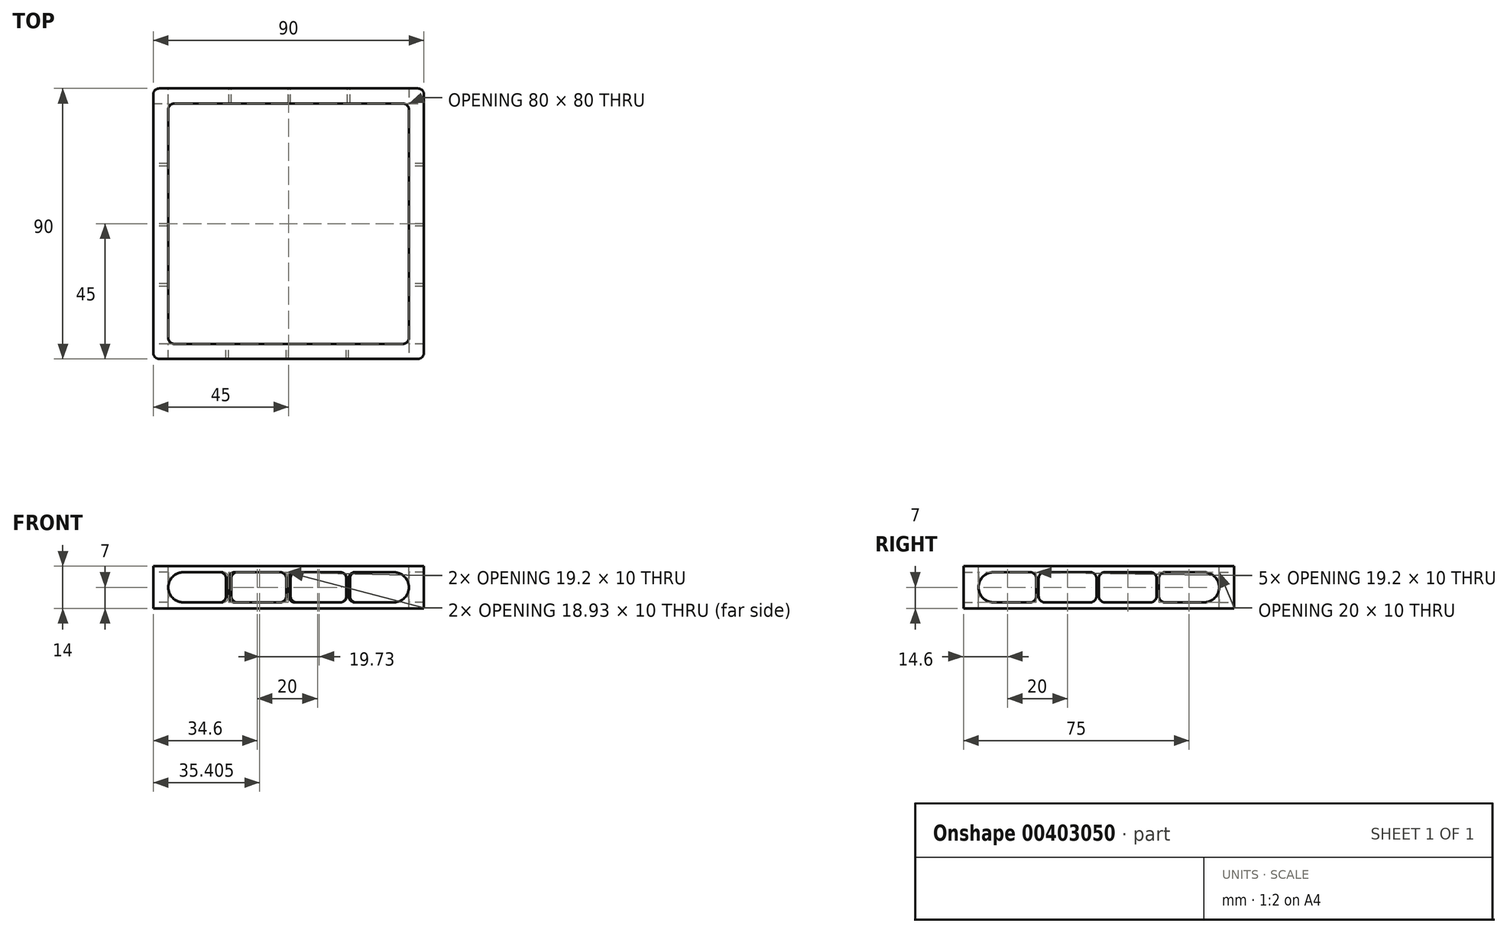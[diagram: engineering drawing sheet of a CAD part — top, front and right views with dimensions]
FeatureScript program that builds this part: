
annotation { "Feature Type Name" : "Feature", "Feature Type Description" : "" }
export const myFeature = defineFeature(function(context is Context, id is Id, definition is map)
    precondition{}
    {
        {
            var Q0;
            Q0=qCreatedBy(makeId("Front.planeOp"),FACE);
            var sketch = newSketch(context, id + "F0", { "sketchPlane" : qUnion([Q0])});
            skLineSegment(sketch, "E0.bottom", {"start": v(-45, 7) * mm, "end": v(45, 7) * mm});
            skLineSegment(sketch, "E0.top", {"start": v(-45, -7) * mm, "end": v(45, -7) * mm});
            skLineSegment(sketch, "E0.left", {"start": v(-45, 7) * mm, "end": v(-45, -7) * mm});
            skLineSegment(sketch, "E0.right", {"start": v(45, 7) * mm, "end": v(45, -7) * mm});
            skPoint(sketch, "E0.middle", {"position": v(0, 0) * mm});
            skSolve(sketch);
        }
        {
            var Q0;
            Q0 = qSketchRegion(id + "F0", true);
            extrude(context, id + "F1", {"entities" : qUnion([Q0]), "endBound" : BoundingType.SYMMETRIC, "depth" : 90 * mm});
        }
        {
            var Q0;
            Q0=makeQuery(id+"F1.opExtrude","CAP_FACE",FACE,{"disambiguationData":[OSD([sQuery(id+"F0.wireOp",EDGE,"E0.bottom"),sQuery(id+"F0.wireOp",EDGE,"E0.top"),sQuery(id+"F0.wireOp",EDGE,"E0.left"),sQuery(id+"F0.wireOp",EDGE,"E0.right")])],"isStart":false});
            var sketch = newSketch(context, id + "F2", { "sketchPlane" : qUnion([Q0])});
            skLineSegment(sketch, "E1.bottom", {"start": v(-40, 5) * mm, "end": v(40, 5) * mm});
            skLineSegment(sketch, "E1.top", {"start": v(-40, -5) * mm, "end": v(40, -5) * mm});
            skLineSegment(sketch, "E1.left", {"start": v(-40, 5) * mm, "end": v(-40, -5) * mm});
            skLineSegment(sketch, "E1.right", {"start": v(40, 5) * mm, "end": v(40, -5) * mm});
            skPoint(sketch, "E1.middle", {"position": v(0, 0) * mm});
            skSolve(sketch);
        }
        {
            var Q0;
            Q0 = qSketchRegion(id + "F2", true);
            extrude(context, id + "F3", {"entities" : qUnion([Q0]), "operationType" : NewBodyOperationType.REMOVE, "oppositeDirection" : true, "depth" : 90 * mm});
        }
        {
            var Q0;
            Q0=makeQuery(id+"F1.opExtrude","SWEPT_FACE",FACE,{"disambiguationData":[OSD([sQuery(id+"F0.wireOp",EDGE,"E0.right")])]});
            var sketch = newSketch(context, id + "F4", { "sketchPlane" : qUnion([Q0])});
            skLineSegment(sketch, "E2.bottom", {"start": v(-40, 5) * mm, "end": v(40, 5) * mm});
            skLineSegment(sketch, "E2.top", {"start": v(-40, -5) * mm, "end": v(40, -5) * mm});
            skLineSegment(sketch, "E2.left", {"start": v(-40, 5) * mm, "end": v(-40, -5) * mm});
            skLineSegment(sketch, "E2.right", {"start": v(40, 5) * mm, "end": v(40, -5) * mm});
            skPoint(sketch, "E2.middle", {"position": v(0, 0) * mm});
            skSolve(sketch);
        }
        {
            var Q0;
            Q0 = qSketchRegion(id + "F4", true);
            extrude(context, id + "F5", {"entities" : qUnion([Q0]), "operationType" : NewBodyOperationType.REMOVE, "oppositeDirection" : true, "depth" : 90 * mm});
        }
        {
            var Q0;
            Q0=makeQuery(id+"F1.opExtrude","SWEPT_FACE",FACE,{"disambiguationData":[OSD([sQuery(id+"F0.wireOp",EDGE,"E0.bottom")])]});
            var sketch = newSketch(context, id + "F6", { "sketchPlane" : qUnion([Q0])});
            skLineSegment(sketch, "E3.bottom", {"start": v(-40, 40) * mm, "end": v(40, 40) * mm});
            skLineSegment(sketch, "E3.top", {"start": v(-40, -40) * mm, "end": v(40, -40) * mm});
            skLineSegment(sketch, "E3.left", {"start": v(-40, 40) * mm, "end": v(-40, -40) * mm});
            skLineSegment(sketch, "E3.right", {"start": v(40, 40) * mm, "end": v(40, -40) * mm});
            skSolve(sketch);
        }
        {
            var Q0;
            Q0 = qSketchRegion(id + "F6", true);
            extrude(context, id + "F7", {"entities" : qUnion([Q0]), "operationType" : NewBodyOperationType.REMOVE, "oppositeDirection" : true, "depth" : 14 * mm});
        }
        {
            var Q0;
            {var subQ3=sQuery(id+"F6.wireOp",EDGE,"E3.bottom");var subQ4=sQuery(id+"F6.wireOp",EDGE,"E3.left");Q0=makeQuery(id+"F7.boolean.opBoolean","COPY",EDGE,{"disambiguationData":[TD([makeQuery(id+"F1.opExtrude","SWEPT_FACE",FACE,{"disambiguationData":[OSD([sQuery(id+"F0.wireOp",EDGE,"E0.bottom")])]})])],"derivedFrom":makeQuery(id+"F7.opExtrude","SWEPT_EDGE",EDGE,{"disambiguationData":[OSD([subQ3,subQ4])]})});}
            var Q1;
            {var subQ3=sQuery(id+"F6.wireOp",EDGE,"E3.bottom");var subQ4=sQuery(id+"F6.wireOp",EDGE,"E3.left");Q1=makeQuery(id+"F7.boolean.opBoolean","COPY",EDGE,{"disambiguationData":[TD([makeQuery(id+"F1.opExtrude","SWEPT_FACE",FACE,{"disambiguationData":[OSD([sQuery(id+"F0.wireOp",EDGE,"E0.top")])]})])],"derivedFrom":makeQuery(id+"F7.opExtrude","SWEPT_EDGE",EDGE,{"disambiguationData":[OSD([subQ3,subQ4])]})});}
            var Q2;
            {var subQ3=sQuery(id+"F6.wireOp",EDGE,"E3.top");var subQ4=sQuery(id+"F6.wireOp",EDGE,"E3.left");Q2=makeQuery(id+"F7.boolean.opBoolean","COPY",EDGE,{"disambiguationData":[TD([makeQuery(id+"F1.opExtrude","SWEPT_FACE",FACE,{"disambiguationData":[OSD([sQuery(id+"F0.wireOp",EDGE,"E0.top")])]})])],"derivedFrom":makeQuery(id+"F7.opExtrude","SWEPT_EDGE",EDGE,{"disambiguationData":[OSD([subQ3,subQ4])]})});}
            var Q3;
            {var subQ3=sQuery(id+"F6.wireOp",EDGE,"E3.top");var subQ4=sQuery(id+"F6.wireOp",EDGE,"E3.left");Q3=makeQuery(id+"F7.boolean.opBoolean","COPY",EDGE,{"disambiguationData":[TD([makeQuery(id+"F1.opExtrude","SWEPT_FACE",FACE,{"disambiguationData":[OSD([sQuery(id+"F0.wireOp",EDGE,"E0.bottom")])]})])],"derivedFrom":makeQuery(id+"F7.opExtrude","SWEPT_EDGE",EDGE,{"disambiguationData":[OSD([subQ3,subQ4])]})});}
            var Q4;
            {var subQ3=sQuery(id+"F6.wireOp",EDGE,"E3.right");var subQ4=sQuery(id+"F6.wireOp",EDGE,"E3.top");Q4=makeQuery(id+"F7.boolean.opBoolean","COPY",EDGE,{"disambiguationData":[TD([makeQuery(id+"F1.opExtrude","SWEPT_FACE",FACE,{"disambiguationData":[OSD([sQuery(id+"F0.wireOp",EDGE,"E0.bottom")])]})])],"derivedFrom":makeQuery(id+"F7.opExtrude","SWEPT_EDGE",EDGE,{"disambiguationData":[OSD([subQ4,subQ3])]})});}
            var Q5;
            {var subQ3=sQuery(id+"F6.wireOp",EDGE,"E3.top");var subQ4=sQuery(id+"F6.wireOp",EDGE,"E3.right");Q5=makeQuery(id+"F7.boolean.opBoolean","COPY",EDGE,{"disambiguationData":[TD([makeQuery(id+"F1.opExtrude","SWEPT_FACE",FACE,{"disambiguationData":[OSD([sQuery(id+"F0.wireOp",EDGE,"E0.top")])]})])],"derivedFrom":makeQuery(id+"F7.opExtrude","SWEPT_EDGE",EDGE,{"disambiguationData":[OSD([subQ3,subQ4])]})});}
            var Q6;
            {var subQ3=sQuery(id+"F6.wireOp",EDGE,"E3.right");var subQ4=sQuery(id+"F6.wireOp",EDGE,"E3.bottom");Q6=makeQuery(id+"F7.boolean.opBoolean","COPY",EDGE,{"disambiguationData":[TD([makeQuery(id+"F1.opExtrude","SWEPT_FACE",FACE,{"disambiguationData":[OSD([sQuery(id+"F0.wireOp",EDGE,"E0.bottom")])]})])],"derivedFrom":makeQuery(id+"F7.opExtrude","SWEPT_EDGE",EDGE,{"disambiguationData":[OSD([subQ4,subQ3])]})});}
            var Q7;
            {var subQ3=sQuery(id+"F6.wireOp",EDGE,"E3.bottom");var subQ4=sQuery(id+"F6.wireOp",EDGE,"E3.right");Q7=makeQuery(id+"F7.boolean.opBoolean","COPY",EDGE,{"disambiguationData":[TD([makeQuery(id+"F1.opExtrude","SWEPT_FACE",FACE,{"disambiguationData":[OSD([sQuery(id+"F0.wireOp",EDGE,"E0.top")])]})])],"derivedFrom":makeQuery(id+"F7.opExtrude","SWEPT_EDGE",EDGE,{"disambiguationData":[OSD([subQ3,subQ4])]})});}
            var Q8;
            Q8=makeQuery(id+"F1.opExtrude","CAP_EDGE",EDGE,{"disambiguationData":[OSD([sQuery(id+"F0.wireOp",EDGE,"E0.left")])],"isStart":false});
            var Q9;
            Q9=makeQuery(id+"F1.opExtrude","CAP_EDGE",EDGE,{"disambiguationData":[OSD([sQuery(id+"F0.wireOp",EDGE,"E0.right")])],"isStart":false});
            var Q10;
            Q10=makeQuery(id+"F1.opExtrude","CAP_EDGE",EDGE,{"disambiguationData":[OSD([sQuery(id+"F0.wireOp",EDGE,"E0.right")])],"isStart":true});
            var Q11;
            Q11=makeQuery(id+"F1.opExtrude","CAP_EDGE",EDGE,{"disambiguationData":[OSD([sQuery(id+"F0.wireOp",EDGE,"E0.left")])],"isStart":true});
            fillet(context, id + "F8", {"entities" : qUnion([Q0, Q1, Q2, Q3, Q4, Q5, Q6, Q7, Q8, Q9, Q10, Q11]), "radius" : 2 * mm, "allowEdgeOverflow" : false});
        }
        {
            var Q0;
            {var subQ0=sQuery(id+"F2.wireOp",EDGE,"E1.top");var subQ1=sQuery(id+"F2.wireOp",EDGE,"E1.right");Q0=makeQuery(id+"F5.boolean.opBoolean","SPLIT",EDGE,{"disambiguationData":[TD([makeQuery(id+"F5.opExtrude","SWEPT_FACE",FACE,{"disambiguationData":[OSD([sQuery(id+"F4.wireOp",EDGE,"E2.left")])]})])],"derivedFrom":makeQuery(id+"F3.boolean.opBoolean","COPY",EDGE,{"derivedFrom":makeQuery(id+"F3.opExtrude","SWEPT_EDGE",EDGE,{"disambiguationData":[OSD([subQ0,subQ1])]})})});}
            var Q1;
            {var subQ0=sQuery(id+"F2.wireOp",EDGE,"E1.bottom");var subQ1=sQuery(id+"F2.wireOp",EDGE,"E1.right");Q1=makeQuery(id+"F5.boolean.opBoolean","SPLIT",EDGE,{"disambiguationData":[TD([makeQuery(id+"F5.opExtrude","SWEPT_FACE",FACE,{"disambiguationData":[OSD([sQuery(id+"F4.wireOp",EDGE,"E2.left")])]})])],"derivedFrom":makeQuery(id+"F3.boolean.opBoolean","COPY",EDGE,{"derivedFrom":makeQuery(id+"F3.opExtrude","SWEPT_EDGE",EDGE,{"disambiguationData":[OSD([subQ0,subQ1])]})})});}
            var Q2;
            {var subQ0=sQuery(id+"F2.wireOp",EDGE,"E1.left");var subQ1=sQuery(id+"F2.wireOp",EDGE,"E1.top");Q2=makeQuery(id+"F5.boolean.opBoolean","SPLIT",EDGE,{"disambiguationData":[TD([makeQuery(id+"F5.opExtrude","SWEPT_FACE",FACE,{"disambiguationData":[OSD([sQuery(id+"F4.wireOp",EDGE,"E2.left")])]})])],"derivedFrom":makeQuery(id+"F3.boolean.opBoolean","COPY",EDGE,{"derivedFrom":makeQuery(id+"F3.opExtrude","SWEPT_EDGE",EDGE,{"disambiguationData":[OSD([subQ1,subQ0])]})})});}
            var Q3;
            {var subQ0=sQuery(id+"F2.wireOp",EDGE,"E1.left");var subQ1=sQuery(id+"F2.wireOp",EDGE,"E1.bottom");Q3=makeQuery(id+"F5.boolean.opBoolean","SPLIT",EDGE,{"disambiguationData":[TD([makeQuery(id+"F5.opExtrude","SWEPT_FACE",FACE,{"disambiguationData":[OSD([sQuery(id+"F4.wireOp",EDGE,"E2.left")])]})])],"derivedFrom":makeQuery(id+"F3.boolean.opBoolean","COPY",EDGE,{"derivedFrom":makeQuery(id+"F3.opExtrude","SWEPT_EDGE",EDGE,{"disambiguationData":[OSD([subQ1,subQ0])]})})});}
            var Q4;
            {var subQ0=sQuery(id+"F4.wireOp",EDGE,"E2.top");var subQ1=sQuery(id+"F4.wireOp",EDGE,"E2.left");Q4=makeQuery(id+"F5.boolean.opBoolean","COPY",EDGE,{"disambiguationData":[TD([makeQuery(id+"F1.opExtrude","SWEPT_FACE",FACE,{"disambiguationData":[OSD([sQuery(id+"F0.wireOp",EDGE,"E0.right")])]})])],"derivedFrom":makeQuery(id+"F5.opExtrude","SWEPT_EDGE",EDGE,{"disambiguationData":[OSD([subQ0,subQ1])]})});}
            var Q5;
            {var subQ0=sQuery(id+"F4.wireOp",EDGE,"E2.bottom");var subQ1=sQuery(id+"F4.wireOp",EDGE,"E2.left");Q5=makeQuery(id+"F5.boolean.opBoolean","COPY",EDGE,{"disambiguationData":[TD([makeQuery(id+"F1.opExtrude","SWEPT_FACE",FACE,{"disambiguationData":[OSD([sQuery(id+"F0.wireOp",EDGE,"E0.right")])]})])],"derivedFrom":makeQuery(id+"F5.opExtrude","SWEPT_EDGE",EDGE,{"disambiguationData":[OSD([subQ0,subQ1])]})});}
            var Q6;
            {var subQ0=sQuery(id+"F4.wireOp",EDGE,"E2.top");var subQ1=sQuery(id+"F4.wireOp",EDGE,"E2.right");Q6=makeQuery(id+"F5.boolean.opBoolean","COPY",EDGE,{"disambiguationData":[TD([makeQuery(id+"F1.opExtrude","SWEPT_FACE",FACE,{"disambiguationData":[OSD([sQuery(id+"F0.wireOp",EDGE,"E0.right")])]})])],"derivedFrom":makeQuery(id+"F5.opExtrude","SWEPT_EDGE",EDGE,{"disambiguationData":[OSD([subQ0,subQ1])]})});}
            var Q7;
            {var subQ0=sQuery(id+"F4.wireOp",EDGE,"E2.bottom");var subQ1=sQuery(id+"F4.wireOp",EDGE,"E2.right");Q7=makeQuery(id+"F5.boolean.opBoolean","COPY",EDGE,{"disambiguationData":[TD([makeQuery(id+"F1.opExtrude","SWEPT_FACE",FACE,{"disambiguationData":[OSD([sQuery(id+"F0.wireOp",EDGE,"E0.right")])]})])],"derivedFrom":makeQuery(id+"F5.opExtrude","SWEPT_EDGE",EDGE,{"disambiguationData":[OSD([subQ0,subQ1])]})});}
            var Q8;
            {var subQ0=sQuery(id+"F2.wireOp",EDGE,"E1.right");var subQ1=sQuery(id+"F2.wireOp",EDGE,"E1.top");Q8=makeQuery(id+"F5.boolean.opBoolean","SPLIT",EDGE,{"disambiguationData":[TD([makeQuery(id+"F5.opExtrude","SWEPT_FACE",FACE,{"disambiguationData":[OSD([sQuery(id+"F4.wireOp",EDGE,"E2.right")])]})])],"derivedFrom":makeQuery(id+"F3.boolean.opBoolean","COPY",EDGE,{"derivedFrom":makeQuery(id+"F3.opExtrude","SWEPT_EDGE",EDGE,{"disambiguationData":[OSD([subQ1,subQ0])]})})});}
            var Q9;
            {var subQ0=sQuery(id+"F2.wireOp",EDGE,"E1.right");var subQ1=sQuery(id+"F2.wireOp",EDGE,"E1.bottom");Q9=makeQuery(id+"F5.boolean.opBoolean","SPLIT",EDGE,{"disambiguationData":[TD([makeQuery(id+"F5.opExtrude","SWEPT_FACE",FACE,{"disambiguationData":[OSD([sQuery(id+"F4.wireOp",EDGE,"E2.right")])]})])],"derivedFrom":makeQuery(id+"F3.boolean.opBoolean","COPY",EDGE,{"derivedFrom":makeQuery(id+"F3.opExtrude","SWEPT_EDGE",EDGE,{"disambiguationData":[OSD([subQ1,subQ0])]})})});}
            var Q10;
            {var subQ0=sQuery(id+"F2.wireOp",EDGE,"E1.top");var subQ1=sQuery(id+"F2.wireOp",EDGE,"E1.left");Q10=makeQuery(id+"F5.boolean.opBoolean","SPLIT",EDGE,{"disambiguationData":[TD([makeQuery(id+"F5.opExtrude","SWEPT_FACE",FACE,{"disambiguationData":[OSD([sQuery(id+"F4.wireOp",EDGE,"E2.right")])]})])],"derivedFrom":makeQuery(id+"F3.boolean.opBoolean","COPY",EDGE,{"derivedFrom":makeQuery(id+"F3.opExtrude","SWEPT_EDGE",EDGE,{"disambiguationData":[OSD([subQ0,subQ1])]})})});}
            var Q11;
            {var subQ0=sQuery(id+"F4.wireOp",EDGE,"E2.top");var subQ1=sQuery(id+"F4.wireOp",EDGE,"E2.right");Q11=makeQuery(id+"F5.boolean.opBoolean","COPY",EDGE,{"disambiguationData":[TD([makeQuery(id+"F1.opExtrude","SWEPT_FACE",FACE,{"disambiguationData":[OSD([sQuery(id+"F0.wireOp",EDGE,"E0.left")])]})])],"derivedFrom":makeQuery(id+"F5.opExtrude","SWEPT_EDGE",EDGE,{"disambiguationData":[OSD([subQ0,subQ1])]})});}
            var Q12;
            {var subQ0=sQuery(id+"F4.wireOp",EDGE,"E2.top");var subQ1=sQuery(id+"F4.wireOp",EDGE,"E2.left");Q12=makeQuery(id+"F5.boolean.opBoolean","COPY",EDGE,{"disambiguationData":[TD([makeQuery(id+"F1.opExtrude","SWEPT_FACE",FACE,{"disambiguationData":[OSD([sQuery(id+"F0.wireOp",EDGE,"E0.left")])]})])],"derivedFrom":makeQuery(id+"F5.opExtrude","SWEPT_EDGE",EDGE,{"disambiguationData":[OSD([subQ0,subQ1])]})});}
            var Q13;
            {var subQ0=sQuery(id+"F4.wireOp",EDGE,"E2.bottom");var subQ1=sQuery(id+"F4.wireOp",EDGE,"E2.left");Q13=makeQuery(id+"F5.boolean.opBoolean","COPY",EDGE,{"disambiguationData":[TD([makeQuery(id+"F1.opExtrude","SWEPT_FACE",FACE,{"disambiguationData":[OSD([sQuery(id+"F0.wireOp",EDGE,"E0.left")])]})])],"derivedFrom":makeQuery(id+"F5.opExtrude","SWEPT_EDGE",EDGE,{"disambiguationData":[OSD([subQ0,subQ1])]})});}
            var Q14;
            {var subQ0=sQuery(id+"F2.wireOp",EDGE,"E1.bottom");var subQ1=sQuery(id+"F2.wireOp",EDGE,"E1.left");Q14=makeQuery(id+"F5.boolean.opBoolean","SPLIT",EDGE,{"disambiguationData":[TD([makeQuery(id+"F5.opExtrude","SWEPT_FACE",FACE,{"disambiguationData":[OSD([sQuery(id+"F4.wireOp",EDGE,"E2.right")])]})])],"derivedFrom":makeQuery(id+"F3.boolean.opBoolean","COPY",EDGE,{"derivedFrom":makeQuery(id+"F3.opExtrude","SWEPT_EDGE",EDGE,{"disambiguationData":[OSD([subQ0,subQ1])]})})});}
            var Q15;
            {var subQ0=sQuery(id+"F4.wireOp",EDGE,"E2.bottom");var subQ1=sQuery(id+"F4.wireOp",EDGE,"E2.right");Q15=makeQuery(id+"F5.boolean.opBoolean","COPY",EDGE,{"disambiguationData":[TD([makeQuery(id+"F1.opExtrude","SWEPT_FACE",FACE,{"disambiguationData":[OSD([sQuery(id+"F0.wireOp",EDGE,"E0.left")])]})])],"derivedFrom":makeQuery(id+"F5.opExtrude","SWEPT_EDGE",EDGE,{"disambiguationData":[OSD([subQ0,subQ1])]})});}
            fillet(context, id + "F9", {"entities" : qUnion([Q0, Q1, Q2, Q3, Q4, Q5, Q6, Q7, Q8, Q9, Q10, Q11, Q12, Q13, Q14, Q15]), "radius" : 5 * mm, "tangentPropagation" : true, "allowEdgeOverflow" : false});
        }
        {
            var Q0;
            Q0=makeQuery(id+"F1.opExtrude","SWEPT_FACE",FACE,{"disambiguationData":[OSD([sQuery(id+"F0.wireOp",EDGE,"E0.bottom")])]});
            var sketch = newSketch(context, id + "F10", { "sketchPlane" : qUnion([Q0])});
            skLineSegment(sketch, "E4.bottom", {"start": v(19.2, -40) * mm, "end": v(20, -40) * mm});
            skLineSegment(sketch, "E4.top", {"start": v(19.2, -45) * mm, "end": v(20, -45) * mm});
            skLineSegment(sketch, "E4.left", {"start": v(19.2, -40) * mm, "end": v(19.2, -45) * mm});
            skLineSegment(sketch, "E4.right", {"start": v(20, -40) * mm, "end": v(20, -45) * mm});
            skLineSegment(sketch, "E5.1.0.0", {"start": v(-0.8, -40) * mm, "end": v(-0.8, -45) * mm});
            skLineSegment(sketch, "E5.1.0.1", {"start": v(0, -40) * mm, "end": v(0, -45) * mm});
            skLineSegment(sketch, "E5.1.0.2", {"start": v(-0.8, -45) * mm, "end": v(0, -45) * mm});
            skLineSegment(sketch, "E5.1.0.3", {"start": v(-0.8, -40) * mm, "end": v(0, -40) * mm});
            skLineSegment(sketch, "E5.2.0.0", {"start": v(-20.8, -40) * mm, "end": v(-20.8, -45) * mm});
            skLineSegment(sketch, "E5.2.0.1", {"start": v(-20, -40) * mm, "end": v(-20, -45) * mm});
            skLineSegment(sketch, "E5.2.0.2", {"start": v(-20.8, -45) * mm, "end": v(-20, -45) * mm});
            skLineSegment(sketch, "E5.2.0.3", {"start": v(-20.8, -40) * mm, "end": v(-20, -40) * mm});
            skLineSegment(sketch, "E5.direction1", {"start": v(19.2, -45) * mm, "end": v(-0.8, -45) * mm, "construction": true});
            skLineSegment(sketch, "E6.0.1.0", {"start": v(19.6, 40) * mm, "end": v(-0.13, 40) * mm, "construction": true});
            skLineSegment(sketch, "E6.0.1.1", {"start": v(19.6, 40) * mm, "end": v(20.4, 40) * mm});
            skLineSegment(sketch, "E6.0.1.2", {"start": v(19.6, 45) * mm, "end": v(19.6, 40) * mm});
            skLineSegment(sketch, "E6.0.1.3", {"start": v(20.4, 45) * mm, "end": v(20.4, 40) * mm});
            skLineSegment(sketch, "E6.0.1.4", {"start": v(-29.6, 40) * mm, "end": v(-29.2, 40) * mm});
            skLineSegment(sketch, "E6.0.1.5", {"start": v(-29.6, 45) * mm, "end": v(-29.2, 45) * mm});
            skLineSegment(sketch, "E6.0.1.6", {"start": v(19.6, 45) * mm, "end": v(20.4, 45) * mm});
            skLineSegment(sketch, "E6.0.1.7", {"start": v(0.67, 45) * mm, "end": v(0.67, 40) * mm});
            skLineSegment(sketch, "E6.0.1.8", {"start": v(-0.13, 45) * mm, "end": v(0.67, 45) * mm});
            skLineSegment(sketch, "E6.0.1.9", {"start": v(-19.06, 45) * mm, "end": v(-19.06, 40) * mm});
            skLineSegment(sketch, "E6.0.1.10", {"start": v(-19.86, 40) * mm, "end": v(-19.06, 40) * mm});
            skLineSegment(sketch, "E6.0.1.11", {"start": v(-19.86, 45) * mm, "end": v(-19.06, 45) * mm});
            skLineSegment(sketch, "E6.0.1.14", {"start": v(-0.13, 45) * mm, "end": v(-0.13, 40) * mm});
            skLineSegment(sketch, "E6.0.1.15", {"start": v(-0.13, 40) * mm, "end": v(0.67, 40) * mm});
            skLineSegment(sketch, "E6.0.1.16", {"start": v(-19.86, 45) * mm, "end": v(-19.86, 40) * mm});
            skLineSegment(sketch, "E6.direction1", {"start": v(-29.6, -45) * mm, "end": v(-5, -45) * mm, "construction": true});
            skLineSegment(sketch, "E7.bottom", {"start": v(40, 19.2) * mm, "end": v(45, 19.2) * mm});
            skLineSegment(sketch, "E7.top", {"start": v(40, 20) * mm, "end": v(45, 20) * mm});
            skLineSegment(sketch, "E7.left", {"start": v(40, 19.2) * mm, "end": v(40, 20) * mm});
            skLineSegment(sketch, "E7.right", {"start": v(45, 19.2) * mm, "end": v(45, 20) * mm});
            skLineSegment(sketch, "E8.0.1.0", {"start": v(40, 0) * mm, "end": v(45, 0) * mm});
            skLineSegment(sketch, "E8.0.1.1", {"start": v(40, -0.8) * mm, "end": v(45, -0.8) * mm});
            skLineSegment(sketch, "E8.0.1.2", {"start": v(45, -0.8) * mm, "end": v(45, 0) * mm});
            skLineSegment(sketch, "E8.0.1.3", {"start": v(40, -0.8) * mm, "end": v(40, 0) * mm});
            skLineSegment(sketch, "E8.0.2.0", {"start": v(40, -20) * mm, "end": v(45, -20) * mm});
            skLineSegment(sketch, "E8.0.2.1", {"start": v(40, -20.8) * mm, "end": v(45, -20.8) * mm});
            skLineSegment(sketch, "E8.0.2.2", {"start": v(45, -20.8) * mm, "end": v(45, -20) * mm});
            skLineSegment(sketch, "E8.0.2.3", {"start": v(40, -20.8) * mm, "end": v(40, -20) * mm});
            skLineSegment(sketch, "E8.1.0.0", {"start": v(-45, 20) * mm, "end": v(-40, 20) * mm});
            skLineSegment(sketch, "E8.1.0.1", {"start": v(-45, 19.2) * mm, "end": v(-40, 19.2) * mm});
            skLineSegment(sketch, "E8.1.0.2", {"start": v(-40, 19.2) * mm, "end": v(-40, 20) * mm});
            skLineSegment(sketch, "E8.1.0.3", {"start": v(-45, 19.2) * mm, "end": v(-45, 20) * mm});
            skLineSegment(sketch, "E8.1.1.0", {"start": v(-45, 0) * mm, "end": v(-40, 0) * mm});
            skLineSegment(sketch, "E8.1.1.1", {"start": v(-45, -0.8) * mm, "end": v(-40, -0.8) * mm});
            skLineSegment(sketch, "E8.1.1.2", {"start": v(-40, -0.8) * mm, "end": v(-40, 0) * mm});
            skLineSegment(sketch, "E8.1.1.3", {"start": v(-45, -0.8) * mm, "end": v(-45, 0) * mm});
            skLineSegment(sketch, "E8.1.2.0", {"start": v(-45, -20) * mm, "end": v(-40, -20) * mm});
            skLineSegment(sketch, "E8.1.2.1", {"start": v(-45, -20.8) * mm, "end": v(-40, -20.8) * mm});
            skLineSegment(sketch, "E8.1.2.2", {"start": v(-40, -20.8) * mm, "end": v(-40, -20) * mm});
            skLineSegment(sketch, "E8.1.2.3", {"start": v(-45, -20.8) * mm, "end": v(-45, -20) * mm});
            skLineSegment(sketch, "E8.direction1", {"start": v(40, 19.2) * mm, "end": v(-45, 19.2) * mm, "construction": true});
            skLineSegment(sketch, "E8.direction2", {"start": v(40, 19.2) * mm, "end": v(40, -0.8) * mm, "construction": true});
            skSolve(sketch);
        }
        {
            var Q0;
            Q0 = qSketchRegion(id + "F10", true);
            extrude(context, id + "F11", {"entities" : qUnion([Q0]), "operationType" : NewBodyOperationType.ADD, "oppositeDirection" : true, "depth" : 14 * mm});
        }
        {
            var Q0;
            {var subQ1=makeQuery(id+"F5.opExtrude","SWEPT_FACE",FACE,{"disambiguationData":[OSD([sQuery(id+"F4.wireOp",EDGE,"E2.top")])]});var subQ2=makeQuery(id+"F3.boolean.opBoolean","COPY",FACE,{"derivedFrom":makeQuery(id+"F3.opExtrude","SWEPT_FACE",FACE,{"disambiguationData":[OSD([sQuery(id+"F2.wireOp",EDGE,"E1.top")])]})});var subQ3=sQuery(id+"F0.wireOp",EDGE,"E0.left");var subQ4=makeQuery(id+"F1.opExtrude","SWEPT_FACE",FACE,{"disambiguationData":[OSD([subQ3])]});var subQ14=makeQuery(id+"F5.boolean.opBoolean","MERGE",FACE,{"derivedFrom":[subQ2,subQ1]});var subQ16=sQuery(id+"F0.wireOp",EDGE,"E0.right");var subQ17=makeQuery(id+"F1.opExtrude","SWEPT_FACE",FACE,{"disambiguationData":[OSD([subQ16])]});var subQ21=sQuery(id+"F0.wireOp",EDGE,"E0.top");var subQ22=sQuery(id+"F0.wireOp",EDGE,"E0.bottom");Q0=makeQuery(id+"F11.boolean.opBoolean","INTERSECT",EDGE,{"derivedFrom":[makeQuery(id+"F9.opFillet","SPLIT",FACE,{"disambiguationData":[OD(0.0)],"derivedFrom":makeQuery(id+"F8.opFillet","MERGE",FACE,{"derivedFrom":[makeQuery(id+"F7.boolean.opBoolean","SPLIT",FACE,{"disambiguationData":[TD([makeQuery(id+"F1.opExtrude","CAP_FACE",FACE,{"disambiguationData":[OSD([subQ22,subQ21,subQ3,subQ16])],"isStart":false})])],"derivedFrom":subQ14}),makeQuery(id+"F7.boolean.opBoolean","SPLIT",FACE,{"disambiguationData":[TD([makeQuery(id+"F1.opExtrude","CAP_FACE",FACE,{"disambiguationData":[OSD([subQ22,subQ21,subQ3,subQ16])],"isStart":true})])],"derivedFrom":subQ14}),makeQuery(id+"F7.boolean.opBoolean","SPLIT",FACE,{"disambiguationData":[TD([subQ17])],"derivedFrom":subQ14}),makeQuery(id+"F7.boolean.opBoolean","SPLIT",FACE,{"disambiguationData":[TD([subQ4])],"derivedFrom":subQ14})]})}),makeQuery(id+"F11.opExtrude","SWEPT_FACE",FACE,{"disambiguationData":[OSD([sQuery(id+"F10.wireOp",EDGE,"E4.right")])]})]});}
            var Q1;
            {var subQ1=makeQuery(id+"F5.opExtrude","SWEPT_FACE",FACE,{"disambiguationData":[OSD([sQuery(id+"F4.wireOp",EDGE,"E2.top")])]});var subQ2=makeQuery(id+"F3.boolean.opBoolean","COPY",FACE,{"derivedFrom":makeQuery(id+"F3.opExtrude","SWEPT_FACE",FACE,{"disambiguationData":[OSD([sQuery(id+"F2.wireOp",EDGE,"E1.top")])]})});var subQ3=sQuery(id+"F0.wireOp",EDGE,"E0.left");var subQ4=makeQuery(id+"F1.opExtrude","SWEPT_FACE",FACE,{"disambiguationData":[OSD([subQ3])]});var subQ14=makeQuery(id+"F5.boolean.opBoolean","MERGE",FACE,{"derivedFrom":[subQ2,subQ1]});var subQ16=sQuery(id+"F0.wireOp",EDGE,"E0.right");var subQ17=makeQuery(id+"F1.opExtrude","SWEPT_FACE",FACE,{"disambiguationData":[OSD([subQ16])]});var subQ21=sQuery(id+"F0.wireOp",EDGE,"E0.top");var subQ22=sQuery(id+"F0.wireOp",EDGE,"E0.bottom");Q1=makeQuery(id+"F11.boolean.opBoolean","INTERSECT",EDGE,{"derivedFrom":[makeQuery(id+"F9.opFillet","SPLIT",FACE,{"disambiguationData":[OD(0.0)],"derivedFrom":makeQuery(id+"F8.opFillet","MERGE",FACE,{"derivedFrom":[makeQuery(id+"F7.boolean.opBoolean","SPLIT",FACE,{"disambiguationData":[TD([makeQuery(id+"F1.opExtrude","CAP_FACE",FACE,{"disambiguationData":[OSD([subQ22,subQ21,subQ3,subQ16])],"isStart":false})])],"derivedFrom":subQ14}),makeQuery(id+"F7.boolean.opBoolean","SPLIT",FACE,{"disambiguationData":[TD([makeQuery(id+"F1.opExtrude","CAP_FACE",FACE,{"disambiguationData":[OSD([subQ22,subQ21,subQ3,subQ16])],"isStart":true})])],"derivedFrom":subQ14}),makeQuery(id+"F7.boolean.opBoolean","SPLIT",FACE,{"disambiguationData":[TD([subQ17])],"derivedFrom":subQ14}),makeQuery(id+"F7.boolean.opBoolean","SPLIT",FACE,{"disambiguationData":[TD([subQ4])],"derivedFrom":subQ14})]})}),makeQuery(id+"F11.opExtrude","SWEPT_FACE",FACE,{"disambiguationData":[OSD([sQuery(id+"F10.wireOp",EDGE,"E5.1.0.1")])]})]});}
            var Q2;
            {var subQ1=makeQuery(id+"F5.opExtrude","SWEPT_FACE",FACE,{"disambiguationData":[OSD([sQuery(id+"F4.wireOp",EDGE,"E2.top")])]});var subQ2=makeQuery(id+"F3.boolean.opBoolean","COPY",FACE,{"derivedFrom":makeQuery(id+"F3.opExtrude","SWEPT_FACE",FACE,{"disambiguationData":[OSD([sQuery(id+"F2.wireOp",EDGE,"E1.top")])]})});var subQ3=sQuery(id+"F0.wireOp",EDGE,"E0.left");var subQ4=makeQuery(id+"F1.opExtrude","SWEPT_FACE",FACE,{"disambiguationData":[OSD([subQ3])]});var subQ14=makeQuery(id+"F5.boolean.opBoolean","MERGE",FACE,{"derivedFrom":[subQ2,subQ1]});var subQ16=sQuery(id+"F0.wireOp",EDGE,"E0.right");var subQ17=makeQuery(id+"F1.opExtrude","SWEPT_FACE",FACE,{"disambiguationData":[OSD([subQ16])]});var subQ21=sQuery(id+"F0.wireOp",EDGE,"E0.top");var subQ22=sQuery(id+"F0.wireOp",EDGE,"E0.bottom");Q2=makeQuery(id+"F11.boolean.opBoolean","INTERSECT",EDGE,{"derivedFrom":[makeQuery(id+"F9.opFillet","SPLIT",FACE,{"disambiguationData":[OD(0.0)],"derivedFrom":makeQuery(id+"F8.opFillet","MERGE",FACE,{"derivedFrom":[makeQuery(id+"F7.boolean.opBoolean","SPLIT",FACE,{"disambiguationData":[TD([makeQuery(id+"F1.opExtrude","CAP_FACE",FACE,{"disambiguationData":[OSD([subQ22,subQ21,subQ3,subQ16])],"isStart":false})])],"derivedFrom":subQ14}),makeQuery(id+"F7.boolean.opBoolean","SPLIT",FACE,{"disambiguationData":[TD([makeQuery(id+"F1.opExtrude","CAP_FACE",FACE,{"disambiguationData":[OSD([subQ22,subQ21,subQ3,subQ16])],"isStart":true})])],"derivedFrom":subQ14}),makeQuery(id+"F7.boolean.opBoolean","SPLIT",FACE,{"disambiguationData":[TD([subQ17])],"derivedFrom":subQ14}),makeQuery(id+"F7.boolean.opBoolean","SPLIT",FACE,{"disambiguationData":[TD([subQ4])],"derivedFrom":subQ14})]})}),makeQuery(id+"F11.opExtrude","SWEPT_FACE",FACE,{"disambiguationData":[OSD([sQuery(id+"F10.wireOp",EDGE,"E5.2.0.1")])]})]});}
            var Q3;
            {var subQ1=makeQuery(id+"F5.opExtrude","SWEPT_FACE",FACE,{"disambiguationData":[OSD([sQuery(id+"F4.wireOp",EDGE,"E2.top")])]});var subQ2=makeQuery(id+"F3.boolean.opBoolean","COPY",FACE,{"derivedFrom":makeQuery(id+"F3.opExtrude","SWEPT_FACE",FACE,{"disambiguationData":[OSD([sQuery(id+"F2.wireOp",EDGE,"E1.top")])]})});var subQ3=sQuery(id+"F0.wireOp",EDGE,"E0.left");var subQ4=makeQuery(id+"F1.opExtrude","SWEPT_FACE",FACE,{"disambiguationData":[OSD([subQ3])]});var subQ14=makeQuery(id+"F5.boolean.opBoolean","MERGE",FACE,{"derivedFrom":[subQ2,subQ1]});var subQ16=sQuery(id+"F0.wireOp",EDGE,"E0.right");var subQ17=makeQuery(id+"F1.opExtrude","SWEPT_FACE",FACE,{"disambiguationData":[OSD([subQ16])]});var subQ21=sQuery(id+"F0.wireOp",EDGE,"E0.top");var subQ22=sQuery(id+"F0.wireOp",EDGE,"E0.bottom");Q3=makeQuery(id+"F11.boolean.opBoolean","INTERSECT",EDGE,{"derivedFrom":[makeQuery(id+"F9.opFillet","SPLIT",FACE,{"disambiguationData":[OD(1.0)],"derivedFrom":makeQuery(id+"F8.opFillet","MERGE",FACE,{"derivedFrom":[makeQuery(id+"F7.boolean.opBoolean","SPLIT",FACE,{"disambiguationData":[TD([makeQuery(id+"F1.opExtrude","CAP_FACE",FACE,{"disambiguationData":[OSD([subQ22,subQ21,subQ3,subQ16])],"isStart":false})])],"derivedFrom":subQ14}),makeQuery(id+"F7.boolean.opBoolean","SPLIT",FACE,{"disambiguationData":[TD([makeQuery(id+"F1.opExtrude","CAP_FACE",FACE,{"disambiguationData":[OSD([subQ22,subQ21,subQ3,subQ16])],"isStart":true})])],"derivedFrom":subQ14}),makeQuery(id+"F7.boolean.opBoolean","SPLIT",FACE,{"disambiguationData":[TD([subQ17])],"derivedFrom":subQ14}),makeQuery(id+"F7.boolean.opBoolean","SPLIT",FACE,{"disambiguationData":[TD([subQ4])],"derivedFrom":subQ14})]})}),makeQuery(id+"F11.opExtrude","SWEPT_FACE",FACE,{"disambiguationData":[OSD([sQuery(id+"F10.wireOp",EDGE,"E6.0.1.9")])]})]});}
            var Q4;
            {var subQ1=makeQuery(id+"F5.opExtrude","SWEPT_FACE",FACE,{"disambiguationData":[OSD([sQuery(id+"F4.wireOp",EDGE,"E2.top")])]});var subQ2=makeQuery(id+"F3.boolean.opBoolean","COPY",FACE,{"derivedFrom":makeQuery(id+"F3.opExtrude","SWEPT_FACE",FACE,{"disambiguationData":[OSD([sQuery(id+"F2.wireOp",EDGE,"E1.top")])]})});var subQ3=sQuery(id+"F0.wireOp",EDGE,"E0.left");var subQ4=makeQuery(id+"F1.opExtrude","SWEPT_FACE",FACE,{"disambiguationData":[OSD([subQ3])]});var subQ14=makeQuery(id+"F5.boolean.opBoolean","MERGE",FACE,{"derivedFrom":[subQ2,subQ1]});var subQ16=sQuery(id+"F0.wireOp",EDGE,"E0.right");var subQ17=makeQuery(id+"F1.opExtrude","SWEPT_FACE",FACE,{"disambiguationData":[OSD([subQ16])]});var subQ21=sQuery(id+"F0.wireOp",EDGE,"E0.top");var subQ22=sQuery(id+"F0.wireOp",EDGE,"E0.bottom");Q4=makeQuery(id+"F11.boolean.opBoolean","INTERSECT",EDGE,{"derivedFrom":[makeQuery(id+"F9.opFillet","SPLIT",FACE,{"disambiguationData":[OD(1.0)],"derivedFrom":makeQuery(id+"F8.opFillet","MERGE",FACE,{"derivedFrom":[makeQuery(id+"F7.boolean.opBoolean","SPLIT",FACE,{"disambiguationData":[TD([makeQuery(id+"F1.opExtrude","CAP_FACE",FACE,{"disambiguationData":[OSD([subQ22,subQ21,subQ3,subQ16])],"isStart":false})])],"derivedFrom":subQ14}),makeQuery(id+"F7.boolean.opBoolean","SPLIT",FACE,{"disambiguationData":[TD([makeQuery(id+"F1.opExtrude","CAP_FACE",FACE,{"disambiguationData":[OSD([subQ22,subQ21,subQ3,subQ16])],"isStart":true})])],"derivedFrom":subQ14}),makeQuery(id+"F7.boolean.opBoolean","SPLIT",FACE,{"disambiguationData":[TD([subQ17])],"derivedFrom":subQ14}),makeQuery(id+"F7.boolean.opBoolean","SPLIT",FACE,{"disambiguationData":[TD([subQ4])],"derivedFrom":subQ14})]})}),makeQuery(id+"F11.opExtrude","SWEPT_FACE",FACE,{"disambiguationData":[OSD([sQuery(id+"F10.wireOp",EDGE,"E6.0.1.7")])]})]});}
            var Q5;
            {var subQ0=makeQuery(id+"F5.opExtrude","SWEPT_FACE",FACE,{"disambiguationData":[OSD([sQuery(id+"F4.wireOp",EDGE,"E2.bottom")])]});var subQ2=makeQuery(id+"F3.boolean.opBoolean","COPY",FACE,{"derivedFrom":makeQuery(id+"F3.opExtrude","SWEPT_FACE",FACE,{"disambiguationData":[OSD([sQuery(id+"F2.wireOp",EDGE,"E1.bottom")])]})});var subQ3=sQuery(id+"F0.wireOp",EDGE,"E0.left");var subQ4=makeQuery(id+"F1.opExtrude","SWEPT_FACE",FACE,{"disambiguationData":[OSD([subQ3])]});var subQ14=makeQuery(id+"F5.boolean.opBoolean","MERGE",FACE,{"derivedFrom":[subQ2,subQ0]});var subQ16=sQuery(id+"F0.wireOp",EDGE,"E0.right");var subQ17=makeQuery(id+"F1.opExtrude","SWEPT_FACE",FACE,{"disambiguationData":[OSD([subQ16])]});var subQ21=sQuery(id+"F0.wireOp",EDGE,"E0.top");var subQ22=sQuery(id+"F0.wireOp",EDGE,"E0.bottom");Q5=makeQuery(id+"F11.boolean.opBoolean","INTERSECT",EDGE,{"derivedFrom":[makeQuery(id+"F9.opFillet","SPLIT",FACE,{"disambiguationData":[OD(0.0)],"derivedFrom":makeQuery(id+"F8.opFillet","MERGE",FACE,{"derivedFrom":[makeQuery(id+"F7.boolean.opBoolean","SPLIT",FACE,{"disambiguationData":[TD([makeQuery(id+"F1.opExtrude","CAP_FACE",FACE,{"disambiguationData":[OSD([subQ22,subQ21,subQ3,subQ16])],"isStart":false})])],"derivedFrom":subQ14}),makeQuery(id+"F7.boolean.opBoolean","SPLIT",FACE,{"disambiguationData":[TD([makeQuery(id+"F1.opExtrude","CAP_FACE",FACE,{"disambiguationData":[OSD([subQ22,subQ21,subQ3,subQ16])],"isStart":true})])],"derivedFrom":subQ14}),makeQuery(id+"F7.boolean.opBoolean","SPLIT",FACE,{"disambiguationData":[TD([subQ17])],"derivedFrom":subQ14}),makeQuery(id+"F7.boolean.opBoolean","SPLIT",FACE,{"disambiguationData":[TD([subQ4])],"derivedFrom":subQ14})]})}),makeQuery(id+"F11.opExtrude","SWEPT_FACE",FACE,{"disambiguationData":[OSD([sQuery(id+"F10.wireOp",EDGE,"E4.right")])]})]});}
            var Q6;
            {var subQ0=makeQuery(id+"F5.opExtrude","SWEPT_FACE",FACE,{"disambiguationData":[OSD([sQuery(id+"F4.wireOp",EDGE,"E2.bottom")])]});var subQ2=makeQuery(id+"F3.boolean.opBoolean","COPY",FACE,{"derivedFrom":makeQuery(id+"F3.opExtrude","SWEPT_FACE",FACE,{"disambiguationData":[OSD([sQuery(id+"F2.wireOp",EDGE,"E1.bottom")])]})});var subQ3=sQuery(id+"F0.wireOp",EDGE,"E0.left");var subQ4=makeQuery(id+"F1.opExtrude","SWEPT_FACE",FACE,{"disambiguationData":[OSD([subQ3])]});var subQ14=makeQuery(id+"F5.boolean.opBoolean","MERGE",FACE,{"derivedFrom":[subQ2,subQ0]});var subQ16=sQuery(id+"F0.wireOp",EDGE,"E0.right");var subQ17=makeQuery(id+"F1.opExtrude","SWEPT_FACE",FACE,{"disambiguationData":[OSD([subQ16])]});var subQ21=sQuery(id+"F0.wireOp",EDGE,"E0.top");var subQ22=sQuery(id+"F0.wireOp",EDGE,"E0.bottom");Q6=makeQuery(id+"F11.boolean.opBoolean","INTERSECT",EDGE,{"derivedFrom":[makeQuery(id+"F9.opFillet","SPLIT",FACE,{"disambiguationData":[OD(0.0)],"derivedFrom":makeQuery(id+"F8.opFillet","MERGE",FACE,{"derivedFrom":[makeQuery(id+"F7.boolean.opBoolean","SPLIT",FACE,{"disambiguationData":[TD([makeQuery(id+"F1.opExtrude","CAP_FACE",FACE,{"disambiguationData":[OSD([subQ22,subQ21,subQ3,subQ16])],"isStart":false})])],"derivedFrom":subQ14}),makeQuery(id+"F7.boolean.opBoolean","SPLIT",FACE,{"disambiguationData":[TD([makeQuery(id+"F1.opExtrude","CAP_FACE",FACE,{"disambiguationData":[OSD([subQ22,subQ21,subQ3,subQ16])],"isStart":true})])],"derivedFrom":subQ14}),makeQuery(id+"F7.boolean.opBoolean","SPLIT",FACE,{"disambiguationData":[TD([subQ17])],"derivedFrom":subQ14}),makeQuery(id+"F7.boolean.opBoolean","SPLIT",FACE,{"disambiguationData":[TD([subQ4])],"derivedFrom":subQ14})]})}),makeQuery(id+"F11.opExtrude","SWEPT_FACE",FACE,{"disambiguationData":[OSD([sQuery(id+"F10.wireOp",EDGE,"E5.1.0.1")])]})]});}
            var Q7;
            {var subQ0=makeQuery(id+"F5.opExtrude","SWEPT_FACE",FACE,{"disambiguationData":[OSD([sQuery(id+"F4.wireOp",EDGE,"E2.bottom")])]});var subQ2=makeQuery(id+"F3.boolean.opBoolean","COPY",FACE,{"derivedFrom":makeQuery(id+"F3.opExtrude","SWEPT_FACE",FACE,{"disambiguationData":[OSD([sQuery(id+"F2.wireOp",EDGE,"E1.bottom")])]})});var subQ3=sQuery(id+"F0.wireOp",EDGE,"E0.left");var subQ4=makeQuery(id+"F1.opExtrude","SWEPT_FACE",FACE,{"disambiguationData":[OSD([subQ3])]});var subQ14=makeQuery(id+"F5.boolean.opBoolean","MERGE",FACE,{"derivedFrom":[subQ2,subQ0]});var subQ16=sQuery(id+"F0.wireOp",EDGE,"E0.right");var subQ17=makeQuery(id+"F1.opExtrude","SWEPT_FACE",FACE,{"disambiguationData":[OSD([subQ16])]});var subQ21=sQuery(id+"F0.wireOp",EDGE,"E0.top");var subQ22=sQuery(id+"F0.wireOp",EDGE,"E0.bottom");Q7=makeQuery(id+"F11.boolean.opBoolean","INTERSECT",EDGE,{"derivedFrom":[makeQuery(id+"F9.opFillet","SPLIT",FACE,{"disambiguationData":[OD(0.0)],"derivedFrom":makeQuery(id+"F8.opFillet","MERGE",FACE,{"derivedFrom":[makeQuery(id+"F7.boolean.opBoolean","SPLIT",FACE,{"disambiguationData":[TD([makeQuery(id+"F1.opExtrude","CAP_FACE",FACE,{"disambiguationData":[OSD([subQ22,subQ21,subQ3,subQ16])],"isStart":false})])],"derivedFrom":subQ14}),makeQuery(id+"F7.boolean.opBoolean","SPLIT",FACE,{"disambiguationData":[TD([makeQuery(id+"F1.opExtrude","CAP_FACE",FACE,{"disambiguationData":[OSD([subQ22,subQ21,subQ3,subQ16])],"isStart":true})])],"derivedFrom":subQ14}),makeQuery(id+"F7.boolean.opBoolean","SPLIT",FACE,{"disambiguationData":[TD([subQ17])],"derivedFrom":subQ14}),makeQuery(id+"F7.boolean.opBoolean","SPLIT",FACE,{"disambiguationData":[TD([subQ4])],"derivedFrom":subQ14})]})}),makeQuery(id+"F11.opExtrude","SWEPT_FACE",FACE,{"disambiguationData":[OSD([sQuery(id+"F10.wireOp",EDGE,"E5.2.0.1")])]})]});}
            var Q8;
            {var subQ0=makeQuery(id+"F5.opExtrude","SWEPT_FACE",FACE,{"disambiguationData":[OSD([sQuery(id+"F4.wireOp",EDGE,"E2.bottom")])]});var subQ2=makeQuery(id+"F3.boolean.opBoolean","COPY",FACE,{"derivedFrom":makeQuery(id+"F3.opExtrude","SWEPT_FACE",FACE,{"disambiguationData":[OSD([sQuery(id+"F2.wireOp",EDGE,"E1.bottom")])]})});var subQ3=sQuery(id+"F0.wireOp",EDGE,"E0.left");var subQ4=makeQuery(id+"F1.opExtrude","SWEPT_FACE",FACE,{"disambiguationData":[OSD([subQ3])]});var subQ14=makeQuery(id+"F5.boolean.opBoolean","MERGE",FACE,{"derivedFrom":[subQ2,subQ0]});var subQ16=sQuery(id+"F0.wireOp",EDGE,"E0.right");var subQ17=makeQuery(id+"F1.opExtrude","SWEPT_FACE",FACE,{"disambiguationData":[OSD([subQ16])]});var subQ21=sQuery(id+"F0.wireOp",EDGE,"E0.top");var subQ22=sQuery(id+"F0.wireOp",EDGE,"E0.bottom");Q8=makeQuery(id+"F11.boolean.opBoolean","INTERSECT",EDGE,{"derivedFrom":[makeQuery(id+"F9.opFillet","SPLIT",FACE,{"disambiguationData":[OD(1.0)],"derivedFrom":makeQuery(id+"F8.opFillet","MERGE",FACE,{"derivedFrom":[makeQuery(id+"F7.boolean.opBoolean","SPLIT",FACE,{"disambiguationData":[TD([makeQuery(id+"F1.opExtrude","CAP_FACE",FACE,{"disambiguationData":[OSD([subQ22,subQ21,subQ3,subQ16])],"isStart":false})])],"derivedFrom":subQ14}),makeQuery(id+"F7.boolean.opBoolean","SPLIT",FACE,{"disambiguationData":[TD([makeQuery(id+"F1.opExtrude","CAP_FACE",FACE,{"disambiguationData":[OSD([subQ22,subQ21,subQ3,subQ16])],"isStart":true})])],"derivedFrom":subQ14}),makeQuery(id+"F7.boolean.opBoolean","SPLIT",FACE,{"disambiguationData":[TD([subQ17])],"derivedFrom":subQ14}),makeQuery(id+"F7.boolean.opBoolean","SPLIT",FACE,{"disambiguationData":[TD([subQ4])],"derivedFrom":subQ14})]})}),makeQuery(id+"F11.opExtrude","SWEPT_FACE",FACE,{"disambiguationData":[OSD([sQuery(id+"F10.wireOp",EDGE,"E6.0.1.9")])]})]});}
            var Q9;
            {var subQ0=makeQuery(id+"F5.opExtrude","SWEPT_FACE",FACE,{"disambiguationData":[OSD([sQuery(id+"F4.wireOp",EDGE,"E2.bottom")])]});var subQ2=makeQuery(id+"F3.boolean.opBoolean","COPY",FACE,{"derivedFrom":makeQuery(id+"F3.opExtrude","SWEPT_FACE",FACE,{"disambiguationData":[OSD([sQuery(id+"F2.wireOp",EDGE,"E1.bottom")])]})});var subQ3=sQuery(id+"F0.wireOp",EDGE,"E0.left");var subQ4=makeQuery(id+"F1.opExtrude","SWEPT_FACE",FACE,{"disambiguationData":[OSD([subQ3])]});var subQ14=makeQuery(id+"F5.boolean.opBoolean","MERGE",FACE,{"derivedFrom":[subQ2,subQ0]});var subQ16=sQuery(id+"F0.wireOp",EDGE,"E0.right");var subQ17=makeQuery(id+"F1.opExtrude","SWEPT_FACE",FACE,{"disambiguationData":[OSD([subQ16])]});var subQ21=sQuery(id+"F0.wireOp",EDGE,"E0.top");var subQ22=sQuery(id+"F0.wireOp",EDGE,"E0.bottom");Q9=makeQuery(id+"F11.boolean.opBoolean","INTERSECT",EDGE,{"derivedFrom":[makeQuery(id+"F9.opFillet","SPLIT",FACE,{"disambiguationData":[OD(1.0)],"derivedFrom":makeQuery(id+"F8.opFillet","MERGE",FACE,{"derivedFrom":[makeQuery(id+"F7.boolean.opBoolean","SPLIT",FACE,{"disambiguationData":[TD([makeQuery(id+"F1.opExtrude","CAP_FACE",FACE,{"disambiguationData":[OSD([subQ22,subQ21,subQ3,subQ16])],"isStart":false})])],"derivedFrom":subQ14}),makeQuery(id+"F7.boolean.opBoolean","SPLIT",FACE,{"disambiguationData":[TD([makeQuery(id+"F1.opExtrude","CAP_FACE",FACE,{"disambiguationData":[OSD([subQ22,subQ21,subQ3,subQ16])],"isStart":true})])],"derivedFrom":subQ14}),makeQuery(id+"F7.boolean.opBoolean","SPLIT",FACE,{"disambiguationData":[TD([subQ17])],"derivedFrom":subQ14}),makeQuery(id+"F7.boolean.opBoolean","SPLIT",FACE,{"disambiguationData":[TD([subQ4])],"derivedFrom":subQ14})]})}),makeQuery(id+"F11.opExtrude","SWEPT_FACE",FACE,{"disambiguationData":[OSD([sQuery(id+"F10.wireOp",EDGE,"E6.0.1.7")])]})]});}
            var Q10;
            {var subQ0=makeQuery(id+"F5.opExtrude","SWEPT_FACE",FACE,{"disambiguationData":[OSD([sQuery(id+"F4.wireOp",EDGE,"E2.bottom")])]});var subQ2=makeQuery(id+"F3.boolean.opBoolean","COPY",FACE,{"derivedFrom":makeQuery(id+"F3.opExtrude","SWEPT_FACE",FACE,{"disambiguationData":[OSD([sQuery(id+"F2.wireOp",EDGE,"E1.bottom")])]})});var subQ3=sQuery(id+"F0.wireOp",EDGE,"E0.left");var subQ4=makeQuery(id+"F1.opExtrude","SWEPT_FACE",FACE,{"disambiguationData":[OSD([subQ3])]});var subQ14=makeQuery(id+"F5.boolean.opBoolean","MERGE",FACE,{"derivedFrom":[subQ2,subQ0]});var subQ16=sQuery(id+"F0.wireOp",EDGE,"E0.right");var subQ17=makeQuery(id+"F1.opExtrude","SWEPT_FACE",FACE,{"disambiguationData":[OSD([subQ16])]});var subQ21=sQuery(id+"F0.wireOp",EDGE,"E0.top");var subQ22=sQuery(id+"F0.wireOp",EDGE,"E0.bottom");Q10=makeQuery(id+"F11.boolean.opBoolean","INTERSECT",EDGE,{"derivedFrom":[makeQuery(id+"F9.opFillet","SPLIT",FACE,{"disambiguationData":[OD(2.0)],"derivedFrom":makeQuery(id+"F8.opFillet","MERGE",FACE,{"derivedFrom":[makeQuery(id+"F7.boolean.opBoolean","SPLIT",FACE,{"disambiguationData":[TD([makeQuery(id+"F1.opExtrude","CAP_FACE",FACE,{"disambiguationData":[OSD([subQ22,subQ21,subQ3,subQ16])],"isStart":false})])],"derivedFrom":subQ14}),makeQuery(id+"F7.boolean.opBoolean","SPLIT",FACE,{"disambiguationData":[TD([makeQuery(id+"F1.opExtrude","CAP_FACE",FACE,{"disambiguationData":[OSD([subQ22,subQ21,subQ3,subQ16])],"isStart":true})])],"derivedFrom":subQ14}),makeQuery(id+"F7.boolean.opBoolean","SPLIT",FACE,{"disambiguationData":[TD([subQ17])],"derivedFrom":subQ14}),makeQuery(id+"F7.boolean.opBoolean","SPLIT",FACE,{"disambiguationData":[TD([subQ4])],"derivedFrom":subQ14})]})}),makeQuery(id+"F11.opExtrude","SWEPT_FACE",FACE,{"disambiguationData":[OSD([sQuery(id+"F10.wireOp",EDGE,"E8.0.2.1")])]})]});}
            var Q11;
            {var subQ0=makeQuery(id+"F5.opExtrude","SWEPT_FACE",FACE,{"disambiguationData":[OSD([sQuery(id+"F4.wireOp",EDGE,"E2.bottom")])]});var subQ2=makeQuery(id+"F3.boolean.opBoolean","COPY",FACE,{"derivedFrom":makeQuery(id+"F3.opExtrude","SWEPT_FACE",FACE,{"disambiguationData":[OSD([sQuery(id+"F2.wireOp",EDGE,"E1.bottom")])]})});var subQ3=sQuery(id+"F0.wireOp",EDGE,"E0.left");var subQ4=makeQuery(id+"F1.opExtrude","SWEPT_FACE",FACE,{"disambiguationData":[OSD([subQ3])]});var subQ14=makeQuery(id+"F5.boolean.opBoolean","MERGE",FACE,{"derivedFrom":[subQ2,subQ0]});var subQ16=sQuery(id+"F0.wireOp",EDGE,"E0.right");var subQ17=makeQuery(id+"F1.opExtrude","SWEPT_FACE",FACE,{"disambiguationData":[OSD([subQ16])]});var subQ21=sQuery(id+"F0.wireOp",EDGE,"E0.top");var subQ22=sQuery(id+"F0.wireOp",EDGE,"E0.bottom");Q11=makeQuery(id+"F11.boolean.opBoolean","INTERSECT",EDGE,{"derivedFrom":[makeQuery(id+"F9.opFillet","SPLIT",FACE,{"disambiguationData":[OD(2.0)],"derivedFrom":makeQuery(id+"F8.opFillet","MERGE",FACE,{"derivedFrom":[makeQuery(id+"F7.boolean.opBoolean","SPLIT",FACE,{"disambiguationData":[TD([makeQuery(id+"F1.opExtrude","CAP_FACE",FACE,{"disambiguationData":[OSD([subQ22,subQ21,subQ3,subQ16])],"isStart":false})])],"derivedFrom":subQ14}),makeQuery(id+"F7.boolean.opBoolean","SPLIT",FACE,{"disambiguationData":[TD([makeQuery(id+"F1.opExtrude","CAP_FACE",FACE,{"disambiguationData":[OSD([subQ22,subQ21,subQ3,subQ16])],"isStart":true})])],"derivedFrom":subQ14}),makeQuery(id+"F7.boolean.opBoolean","SPLIT",FACE,{"disambiguationData":[TD([subQ17])],"derivedFrom":subQ14}),makeQuery(id+"F7.boolean.opBoolean","SPLIT",FACE,{"disambiguationData":[TD([subQ4])],"derivedFrom":subQ14})]})}),makeQuery(id+"F11.opExtrude","SWEPT_FACE",FACE,{"disambiguationData":[OSD([sQuery(id+"F10.wireOp",EDGE,"E8.0.1.1")])]})]});}
            var Q12;
            {var subQ0=makeQuery(id+"F5.opExtrude","SWEPT_FACE",FACE,{"disambiguationData":[OSD([sQuery(id+"F4.wireOp",EDGE,"E2.bottom")])]});var subQ2=makeQuery(id+"F3.boolean.opBoolean","COPY",FACE,{"derivedFrom":makeQuery(id+"F3.opExtrude","SWEPT_FACE",FACE,{"disambiguationData":[OSD([sQuery(id+"F2.wireOp",EDGE,"E1.bottom")])]})});var subQ3=sQuery(id+"F0.wireOp",EDGE,"E0.left");var subQ4=makeQuery(id+"F1.opExtrude","SWEPT_FACE",FACE,{"disambiguationData":[OSD([subQ3])]});var subQ14=makeQuery(id+"F5.boolean.opBoolean","MERGE",FACE,{"derivedFrom":[subQ2,subQ0]});var subQ16=sQuery(id+"F0.wireOp",EDGE,"E0.right");var subQ17=makeQuery(id+"F1.opExtrude","SWEPT_FACE",FACE,{"disambiguationData":[OSD([subQ16])]});var subQ21=sQuery(id+"F0.wireOp",EDGE,"E0.top");var subQ22=sQuery(id+"F0.wireOp",EDGE,"E0.bottom");Q12=makeQuery(id+"F11.boolean.opBoolean","INTERSECT",EDGE,{"derivedFrom":[makeQuery(id+"F9.opFillet","SPLIT",FACE,{"disambiguationData":[OD(2.0)],"derivedFrom":makeQuery(id+"F8.opFillet","MERGE",FACE,{"derivedFrom":[makeQuery(id+"F7.boolean.opBoolean","SPLIT",FACE,{"disambiguationData":[TD([makeQuery(id+"F1.opExtrude","CAP_FACE",FACE,{"disambiguationData":[OSD([subQ22,subQ21,subQ3,subQ16])],"isStart":false})])],"derivedFrom":subQ14}),makeQuery(id+"F7.boolean.opBoolean","SPLIT",FACE,{"disambiguationData":[TD([makeQuery(id+"F1.opExtrude","CAP_FACE",FACE,{"disambiguationData":[OSD([subQ22,subQ21,subQ3,subQ16])],"isStart":true})])],"derivedFrom":subQ14}),makeQuery(id+"F7.boolean.opBoolean","SPLIT",FACE,{"disambiguationData":[TD([subQ17])],"derivedFrom":subQ14}),makeQuery(id+"F7.boolean.opBoolean","SPLIT",FACE,{"disambiguationData":[TD([subQ4])],"derivedFrom":subQ14})]})}),makeQuery(id+"F11.opExtrude","SWEPT_FACE",FACE,{"disambiguationData":[OSD([sQuery(id+"F10.wireOp",EDGE,"E7.bottom")])]})]});}
            var Q13;
            {var subQ1=makeQuery(id+"F5.opExtrude","SWEPT_FACE",FACE,{"disambiguationData":[OSD([sQuery(id+"F4.wireOp",EDGE,"E2.top")])]});var subQ2=makeQuery(id+"F3.boolean.opBoolean","COPY",FACE,{"derivedFrom":makeQuery(id+"F3.opExtrude","SWEPT_FACE",FACE,{"disambiguationData":[OSD([sQuery(id+"F2.wireOp",EDGE,"E1.top")])]})});var subQ3=sQuery(id+"F0.wireOp",EDGE,"E0.left");var subQ4=makeQuery(id+"F1.opExtrude","SWEPT_FACE",FACE,{"disambiguationData":[OSD([subQ3])]});var subQ14=makeQuery(id+"F5.boolean.opBoolean","MERGE",FACE,{"derivedFrom":[subQ2,subQ1]});var subQ16=sQuery(id+"F0.wireOp",EDGE,"E0.right");var subQ17=makeQuery(id+"F1.opExtrude","SWEPT_FACE",FACE,{"disambiguationData":[OSD([subQ16])]});var subQ21=sQuery(id+"F0.wireOp",EDGE,"E0.top");var subQ22=sQuery(id+"F0.wireOp",EDGE,"E0.bottom");Q13=makeQuery(id+"F11.boolean.opBoolean","INTERSECT",EDGE,{"derivedFrom":[makeQuery(id+"F9.opFillet","SPLIT",FACE,{"disambiguationData":[OD(2.0)],"derivedFrom":makeQuery(id+"F8.opFillet","MERGE",FACE,{"derivedFrom":[makeQuery(id+"F7.boolean.opBoolean","SPLIT",FACE,{"disambiguationData":[TD([makeQuery(id+"F1.opExtrude","CAP_FACE",FACE,{"disambiguationData":[OSD([subQ22,subQ21,subQ3,subQ16])],"isStart":false})])],"derivedFrom":subQ14}),makeQuery(id+"F7.boolean.opBoolean","SPLIT",FACE,{"disambiguationData":[TD([makeQuery(id+"F1.opExtrude","CAP_FACE",FACE,{"disambiguationData":[OSD([subQ22,subQ21,subQ3,subQ16])],"isStart":true})])],"derivedFrom":subQ14}),makeQuery(id+"F7.boolean.opBoolean","SPLIT",FACE,{"disambiguationData":[TD([subQ17])],"derivedFrom":subQ14}),makeQuery(id+"F7.boolean.opBoolean","SPLIT",FACE,{"disambiguationData":[TD([subQ4])],"derivedFrom":subQ14})]})}),makeQuery(id+"F11.opExtrude","SWEPT_FACE",FACE,{"disambiguationData":[OSD([sQuery(id+"F10.wireOp",EDGE,"E7.bottom")])]})]});}
            var Q14;
            {var subQ1=makeQuery(id+"F5.opExtrude","SWEPT_FACE",FACE,{"disambiguationData":[OSD([sQuery(id+"F4.wireOp",EDGE,"E2.top")])]});var subQ2=makeQuery(id+"F3.boolean.opBoolean","COPY",FACE,{"derivedFrom":makeQuery(id+"F3.opExtrude","SWEPT_FACE",FACE,{"disambiguationData":[OSD([sQuery(id+"F2.wireOp",EDGE,"E1.top")])]})});var subQ3=sQuery(id+"F0.wireOp",EDGE,"E0.left");var subQ4=makeQuery(id+"F1.opExtrude","SWEPT_FACE",FACE,{"disambiguationData":[OSD([subQ3])]});var subQ14=makeQuery(id+"F5.boolean.opBoolean","MERGE",FACE,{"derivedFrom":[subQ2,subQ1]});var subQ16=sQuery(id+"F0.wireOp",EDGE,"E0.right");var subQ17=makeQuery(id+"F1.opExtrude","SWEPT_FACE",FACE,{"disambiguationData":[OSD([subQ16])]});var subQ21=sQuery(id+"F0.wireOp",EDGE,"E0.top");var subQ22=sQuery(id+"F0.wireOp",EDGE,"E0.bottom");Q14=makeQuery(id+"F11.boolean.opBoolean","INTERSECT",EDGE,{"derivedFrom":[makeQuery(id+"F9.opFillet","SPLIT",FACE,{"disambiguationData":[OD(2.0)],"derivedFrom":makeQuery(id+"F8.opFillet","MERGE",FACE,{"derivedFrom":[makeQuery(id+"F7.boolean.opBoolean","SPLIT",FACE,{"disambiguationData":[TD([makeQuery(id+"F1.opExtrude","CAP_FACE",FACE,{"disambiguationData":[OSD([subQ22,subQ21,subQ3,subQ16])],"isStart":false})])],"derivedFrom":subQ14}),makeQuery(id+"F7.boolean.opBoolean","SPLIT",FACE,{"disambiguationData":[TD([makeQuery(id+"F1.opExtrude","CAP_FACE",FACE,{"disambiguationData":[OSD([subQ22,subQ21,subQ3,subQ16])],"isStart":true})])],"derivedFrom":subQ14}),makeQuery(id+"F7.boolean.opBoolean","SPLIT",FACE,{"disambiguationData":[TD([subQ17])],"derivedFrom":subQ14}),makeQuery(id+"F7.boolean.opBoolean","SPLIT",FACE,{"disambiguationData":[TD([subQ4])],"derivedFrom":subQ14})]})}),makeQuery(id+"F11.opExtrude","SWEPT_FACE",FACE,{"disambiguationData":[OSD([sQuery(id+"F10.wireOp",EDGE,"E8.0.1.1")])]})]});}
            var Q15;
            {var subQ1=makeQuery(id+"F5.opExtrude","SWEPT_FACE",FACE,{"disambiguationData":[OSD([sQuery(id+"F4.wireOp",EDGE,"E2.top")])]});var subQ2=makeQuery(id+"F3.boolean.opBoolean","COPY",FACE,{"derivedFrom":makeQuery(id+"F3.opExtrude","SWEPT_FACE",FACE,{"disambiguationData":[OSD([sQuery(id+"F2.wireOp",EDGE,"E1.top")])]})});var subQ3=sQuery(id+"F0.wireOp",EDGE,"E0.left");var subQ4=makeQuery(id+"F1.opExtrude","SWEPT_FACE",FACE,{"disambiguationData":[OSD([subQ3])]});var subQ14=makeQuery(id+"F5.boolean.opBoolean","MERGE",FACE,{"derivedFrom":[subQ2,subQ1]});var subQ16=sQuery(id+"F0.wireOp",EDGE,"E0.right");var subQ17=makeQuery(id+"F1.opExtrude","SWEPT_FACE",FACE,{"disambiguationData":[OSD([subQ16])]});var subQ21=sQuery(id+"F0.wireOp",EDGE,"E0.top");var subQ22=sQuery(id+"F0.wireOp",EDGE,"E0.bottom");Q15=makeQuery(id+"F11.boolean.opBoolean","INTERSECT",EDGE,{"derivedFrom":[makeQuery(id+"F9.opFillet","SPLIT",FACE,{"disambiguationData":[OD(2.0)],"derivedFrom":makeQuery(id+"F8.opFillet","MERGE",FACE,{"derivedFrom":[makeQuery(id+"F7.boolean.opBoolean","SPLIT",FACE,{"disambiguationData":[TD([makeQuery(id+"F1.opExtrude","CAP_FACE",FACE,{"disambiguationData":[OSD([subQ22,subQ21,subQ3,subQ16])],"isStart":false})])],"derivedFrom":subQ14}),makeQuery(id+"F7.boolean.opBoolean","SPLIT",FACE,{"disambiguationData":[TD([makeQuery(id+"F1.opExtrude","CAP_FACE",FACE,{"disambiguationData":[OSD([subQ22,subQ21,subQ3,subQ16])],"isStart":true})])],"derivedFrom":subQ14}),makeQuery(id+"F7.boolean.opBoolean","SPLIT",FACE,{"disambiguationData":[TD([subQ17])],"derivedFrom":subQ14}),makeQuery(id+"F7.boolean.opBoolean","SPLIT",FACE,{"disambiguationData":[TD([subQ4])],"derivedFrom":subQ14})]})}),makeQuery(id+"F11.opExtrude","SWEPT_FACE",FACE,{"disambiguationData":[OSD([sQuery(id+"F10.wireOp",EDGE,"E8.0.2.1")])]})]});}
            var Q16;
            {var subQ0=makeQuery(id+"F5.opExtrude","SWEPT_FACE",FACE,{"disambiguationData":[OSD([sQuery(id+"F4.wireOp",EDGE,"E2.bottom")])]});var subQ2=makeQuery(id+"F3.boolean.opBoolean","COPY",FACE,{"derivedFrom":makeQuery(id+"F3.opExtrude","SWEPT_FACE",FACE,{"disambiguationData":[OSD([sQuery(id+"F2.wireOp",EDGE,"E1.bottom")])]})});var subQ3=sQuery(id+"F0.wireOp",EDGE,"E0.left");var subQ4=makeQuery(id+"F1.opExtrude","SWEPT_FACE",FACE,{"disambiguationData":[OSD([subQ3])]});var subQ14=makeQuery(id+"F5.boolean.opBoolean","MERGE",FACE,{"derivedFrom":[subQ2,subQ0]});var subQ16=sQuery(id+"F0.wireOp",EDGE,"E0.right");var subQ17=makeQuery(id+"F1.opExtrude","SWEPT_FACE",FACE,{"disambiguationData":[OSD([subQ16])]});var subQ21=sQuery(id+"F0.wireOp",EDGE,"E0.top");var subQ22=sQuery(id+"F0.wireOp",EDGE,"E0.bottom");Q16=makeQuery(id+"F11.boolean.opBoolean","INTERSECT",EDGE,{"derivedFrom":[makeQuery(id+"F9.opFillet","SPLIT",FACE,{"disambiguationData":[OD(0.0)],"derivedFrom":makeQuery(id+"F8.opFillet","MERGE",FACE,{"derivedFrom":[makeQuery(id+"F7.boolean.opBoolean","SPLIT",FACE,{"disambiguationData":[TD([makeQuery(id+"F1.opExtrude","CAP_FACE",FACE,{"disambiguationData":[OSD([subQ22,subQ21,subQ3,subQ16])],"isStart":false})])],"derivedFrom":subQ14}),makeQuery(id+"F7.boolean.opBoolean","SPLIT",FACE,{"disambiguationData":[TD([makeQuery(id+"F1.opExtrude","CAP_FACE",FACE,{"disambiguationData":[OSD([subQ22,subQ21,subQ3,subQ16])],"isStart":true})])],"derivedFrom":subQ14}),makeQuery(id+"F7.boolean.opBoolean","SPLIT",FACE,{"disambiguationData":[TD([subQ17])],"derivedFrom":subQ14}),makeQuery(id+"F7.boolean.opBoolean","SPLIT",FACE,{"disambiguationData":[TD([subQ4])],"derivedFrom":subQ14})]})}),makeQuery(id+"F11.opExtrude","SWEPT_FACE",FACE,{"disambiguationData":[OSD([sQuery(id+"F10.wireOp",EDGE,"E4.left")])]})]});}
            var Q17;
            {var subQ0=makeQuery(id+"F5.opExtrude","SWEPT_FACE",FACE,{"disambiguationData":[OSD([sQuery(id+"F4.wireOp",EDGE,"E2.bottom")])]});var subQ2=makeQuery(id+"F3.boolean.opBoolean","COPY",FACE,{"derivedFrom":makeQuery(id+"F3.opExtrude","SWEPT_FACE",FACE,{"disambiguationData":[OSD([sQuery(id+"F2.wireOp",EDGE,"E1.bottom")])]})});var subQ3=sQuery(id+"F0.wireOp",EDGE,"E0.left");var subQ4=makeQuery(id+"F1.opExtrude","SWEPT_FACE",FACE,{"disambiguationData":[OSD([subQ3])]});var subQ14=makeQuery(id+"F5.boolean.opBoolean","MERGE",FACE,{"derivedFrom":[subQ2,subQ0]});var subQ16=sQuery(id+"F0.wireOp",EDGE,"E0.right");var subQ17=makeQuery(id+"F1.opExtrude","SWEPT_FACE",FACE,{"disambiguationData":[OSD([subQ16])]});var subQ21=sQuery(id+"F0.wireOp",EDGE,"E0.top");var subQ22=sQuery(id+"F0.wireOp",EDGE,"E0.bottom");Q17=makeQuery(id+"F11.boolean.opBoolean","INTERSECT",EDGE,{"derivedFrom":[makeQuery(id+"F9.opFillet","SPLIT",FACE,{"disambiguationData":[OD(0.0)],"derivedFrom":makeQuery(id+"F8.opFillet","MERGE",FACE,{"derivedFrom":[makeQuery(id+"F7.boolean.opBoolean","SPLIT",FACE,{"disambiguationData":[TD([makeQuery(id+"F1.opExtrude","CAP_FACE",FACE,{"disambiguationData":[OSD([subQ22,subQ21,subQ3,subQ16])],"isStart":false})])],"derivedFrom":subQ14}),makeQuery(id+"F7.boolean.opBoolean","SPLIT",FACE,{"disambiguationData":[TD([makeQuery(id+"F1.opExtrude","CAP_FACE",FACE,{"disambiguationData":[OSD([subQ22,subQ21,subQ3,subQ16])],"isStart":true})])],"derivedFrom":subQ14}),makeQuery(id+"F7.boolean.opBoolean","SPLIT",FACE,{"disambiguationData":[TD([subQ17])],"derivedFrom":subQ14}),makeQuery(id+"F7.boolean.opBoolean","SPLIT",FACE,{"disambiguationData":[TD([subQ4])],"derivedFrom":subQ14})]})}),makeQuery(id+"F11.opExtrude","SWEPT_FACE",FACE,{"disambiguationData":[OSD([sQuery(id+"F10.wireOp",EDGE,"E5.1.0.0")])]})]});}
            var Q18;
            {var subQ0=makeQuery(id+"F5.opExtrude","SWEPT_FACE",FACE,{"disambiguationData":[OSD([sQuery(id+"F4.wireOp",EDGE,"E2.bottom")])]});var subQ2=makeQuery(id+"F3.boolean.opBoolean","COPY",FACE,{"derivedFrom":makeQuery(id+"F3.opExtrude","SWEPT_FACE",FACE,{"disambiguationData":[OSD([sQuery(id+"F2.wireOp",EDGE,"E1.bottom")])]})});var subQ3=sQuery(id+"F0.wireOp",EDGE,"E0.left");var subQ4=makeQuery(id+"F1.opExtrude","SWEPT_FACE",FACE,{"disambiguationData":[OSD([subQ3])]});var subQ14=makeQuery(id+"F5.boolean.opBoolean","MERGE",FACE,{"derivedFrom":[subQ2,subQ0]});var subQ16=sQuery(id+"F0.wireOp",EDGE,"E0.right");var subQ17=makeQuery(id+"F1.opExtrude","SWEPT_FACE",FACE,{"disambiguationData":[OSD([subQ16])]});var subQ21=sQuery(id+"F0.wireOp",EDGE,"E0.top");var subQ22=sQuery(id+"F0.wireOp",EDGE,"E0.bottom");Q18=makeQuery(id+"F11.boolean.opBoolean","INTERSECT",EDGE,{"derivedFrom":[makeQuery(id+"F9.opFillet","SPLIT",FACE,{"disambiguationData":[OD(0.0)],"derivedFrom":makeQuery(id+"F8.opFillet","MERGE",FACE,{"derivedFrom":[makeQuery(id+"F7.boolean.opBoolean","SPLIT",FACE,{"disambiguationData":[TD([makeQuery(id+"F1.opExtrude","CAP_FACE",FACE,{"disambiguationData":[OSD([subQ22,subQ21,subQ3,subQ16])],"isStart":false})])],"derivedFrom":subQ14}),makeQuery(id+"F7.boolean.opBoolean","SPLIT",FACE,{"disambiguationData":[TD([makeQuery(id+"F1.opExtrude","CAP_FACE",FACE,{"disambiguationData":[OSD([subQ22,subQ21,subQ3,subQ16])],"isStart":true})])],"derivedFrom":subQ14}),makeQuery(id+"F7.boolean.opBoolean","SPLIT",FACE,{"disambiguationData":[TD([subQ17])],"derivedFrom":subQ14}),makeQuery(id+"F7.boolean.opBoolean","SPLIT",FACE,{"disambiguationData":[TD([subQ4])],"derivedFrom":subQ14})]})}),makeQuery(id+"F11.opExtrude","SWEPT_FACE",FACE,{"disambiguationData":[OSD([sQuery(id+"F10.wireOp",EDGE,"E5.2.0.0")])]})]});}
            var Q19;
            {var subQ1=makeQuery(id+"F5.opExtrude","SWEPT_FACE",FACE,{"disambiguationData":[OSD([sQuery(id+"F4.wireOp",EDGE,"E2.top")])]});var subQ2=makeQuery(id+"F3.boolean.opBoolean","COPY",FACE,{"derivedFrom":makeQuery(id+"F3.opExtrude","SWEPT_FACE",FACE,{"disambiguationData":[OSD([sQuery(id+"F2.wireOp",EDGE,"E1.top")])]})});var subQ3=sQuery(id+"F0.wireOp",EDGE,"E0.left");var subQ4=makeQuery(id+"F1.opExtrude","SWEPT_FACE",FACE,{"disambiguationData":[OSD([subQ3])]});var subQ14=makeQuery(id+"F5.boolean.opBoolean","MERGE",FACE,{"derivedFrom":[subQ2,subQ1]});var subQ16=sQuery(id+"F0.wireOp",EDGE,"E0.right");var subQ17=makeQuery(id+"F1.opExtrude","SWEPT_FACE",FACE,{"disambiguationData":[OSD([subQ16])]});var subQ21=sQuery(id+"F0.wireOp",EDGE,"E0.top");var subQ22=sQuery(id+"F0.wireOp",EDGE,"E0.bottom");Q19=makeQuery(id+"F11.boolean.opBoolean","INTERSECT",EDGE,{"derivedFrom":[makeQuery(id+"F9.opFillet","SPLIT",FACE,{"disambiguationData":[OD(0.0)],"derivedFrom":makeQuery(id+"F8.opFillet","MERGE",FACE,{"derivedFrom":[makeQuery(id+"F7.boolean.opBoolean","SPLIT",FACE,{"disambiguationData":[TD([makeQuery(id+"F1.opExtrude","CAP_FACE",FACE,{"disambiguationData":[OSD([subQ22,subQ21,subQ3,subQ16])],"isStart":false})])],"derivedFrom":subQ14}),makeQuery(id+"F7.boolean.opBoolean","SPLIT",FACE,{"disambiguationData":[TD([makeQuery(id+"F1.opExtrude","CAP_FACE",FACE,{"disambiguationData":[OSD([subQ22,subQ21,subQ3,subQ16])],"isStart":true})])],"derivedFrom":subQ14}),makeQuery(id+"F7.boolean.opBoolean","SPLIT",FACE,{"disambiguationData":[TD([subQ17])],"derivedFrom":subQ14}),makeQuery(id+"F7.boolean.opBoolean","SPLIT",FACE,{"disambiguationData":[TD([subQ4])],"derivedFrom":subQ14})]})}),makeQuery(id+"F11.opExtrude","SWEPT_FACE",FACE,{"disambiguationData":[OSD([sQuery(id+"F10.wireOp",EDGE,"E5.2.0.0")])]})]});}
            var Q20;
            {var subQ1=makeQuery(id+"F5.opExtrude","SWEPT_FACE",FACE,{"disambiguationData":[OSD([sQuery(id+"F4.wireOp",EDGE,"E2.top")])]});var subQ2=makeQuery(id+"F3.boolean.opBoolean","COPY",FACE,{"derivedFrom":makeQuery(id+"F3.opExtrude","SWEPT_FACE",FACE,{"disambiguationData":[OSD([sQuery(id+"F2.wireOp",EDGE,"E1.top")])]})});var subQ3=sQuery(id+"F0.wireOp",EDGE,"E0.left");var subQ4=makeQuery(id+"F1.opExtrude","SWEPT_FACE",FACE,{"disambiguationData":[OSD([subQ3])]});var subQ14=makeQuery(id+"F5.boolean.opBoolean","MERGE",FACE,{"derivedFrom":[subQ2,subQ1]});var subQ16=sQuery(id+"F0.wireOp",EDGE,"E0.right");var subQ17=makeQuery(id+"F1.opExtrude","SWEPT_FACE",FACE,{"disambiguationData":[OSD([subQ16])]});var subQ21=sQuery(id+"F0.wireOp",EDGE,"E0.top");var subQ22=sQuery(id+"F0.wireOp",EDGE,"E0.bottom");Q20=makeQuery(id+"F11.boolean.opBoolean","INTERSECT",EDGE,{"derivedFrom":[makeQuery(id+"F9.opFillet","SPLIT",FACE,{"disambiguationData":[OD(0.0)],"derivedFrom":makeQuery(id+"F8.opFillet","MERGE",FACE,{"derivedFrom":[makeQuery(id+"F7.boolean.opBoolean","SPLIT",FACE,{"disambiguationData":[TD([makeQuery(id+"F1.opExtrude","CAP_FACE",FACE,{"disambiguationData":[OSD([subQ22,subQ21,subQ3,subQ16])],"isStart":false})])],"derivedFrom":subQ14}),makeQuery(id+"F7.boolean.opBoolean","SPLIT",FACE,{"disambiguationData":[TD([makeQuery(id+"F1.opExtrude","CAP_FACE",FACE,{"disambiguationData":[OSD([subQ22,subQ21,subQ3,subQ16])],"isStart":true})])],"derivedFrom":subQ14}),makeQuery(id+"F7.boolean.opBoolean","SPLIT",FACE,{"disambiguationData":[TD([subQ17])],"derivedFrom":subQ14}),makeQuery(id+"F7.boolean.opBoolean","SPLIT",FACE,{"disambiguationData":[TD([subQ4])],"derivedFrom":subQ14})]})}),makeQuery(id+"F11.opExtrude","SWEPT_FACE",FACE,{"disambiguationData":[OSD([sQuery(id+"F10.wireOp",EDGE,"E5.1.0.0")])]})]});}
            var Q21;
            {var subQ1=makeQuery(id+"F5.opExtrude","SWEPT_FACE",FACE,{"disambiguationData":[OSD([sQuery(id+"F4.wireOp",EDGE,"E2.top")])]});var subQ2=makeQuery(id+"F3.boolean.opBoolean","COPY",FACE,{"derivedFrom":makeQuery(id+"F3.opExtrude","SWEPT_FACE",FACE,{"disambiguationData":[OSD([sQuery(id+"F2.wireOp",EDGE,"E1.top")])]})});var subQ3=sQuery(id+"F0.wireOp",EDGE,"E0.left");var subQ4=makeQuery(id+"F1.opExtrude","SWEPT_FACE",FACE,{"disambiguationData":[OSD([subQ3])]});var subQ14=makeQuery(id+"F5.boolean.opBoolean","MERGE",FACE,{"derivedFrom":[subQ2,subQ1]});var subQ16=sQuery(id+"F0.wireOp",EDGE,"E0.right");var subQ17=makeQuery(id+"F1.opExtrude","SWEPT_FACE",FACE,{"disambiguationData":[OSD([subQ16])]});var subQ21=sQuery(id+"F0.wireOp",EDGE,"E0.top");var subQ22=sQuery(id+"F0.wireOp",EDGE,"E0.bottom");Q21=makeQuery(id+"F11.boolean.opBoolean","INTERSECT",EDGE,{"derivedFrom":[makeQuery(id+"F9.opFillet","SPLIT",FACE,{"disambiguationData":[OD(0.0)],"derivedFrom":makeQuery(id+"F8.opFillet","MERGE",FACE,{"derivedFrom":[makeQuery(id+"F7.boolean.opBoolean","SPLIT",FACE,{"disambiguationData":[TD([makeQuery(id+"F1.opExtrude","CAP_FACE",FACE,{"disambiguationData":[OSD([subQ22,subQ21,subQ3,subQ16])],"isStart":false})])],"derivedFrom":subQ14}),makeQuery(id+"F7.boolean.opBoolean","SPLIT",FACE,{"disambiguationData":[TD([makeQuery(id+"F1.opExtrude","CAP_FACE",FACE,{"disambiguationData":[OSD([subQ22,subQ21,subQ3,subQ16])],"isStart":true})])],"derivedFrom":subQ14}),makeQuery(id+"F7.boolean.opBoolean","SPLIT",FACE,{"disambiguationData":[TD([subQ17])],"derivedFrom":subQ14}),makeQuery(id+"F7.boolean.opBoolean","SPLIT",FACE,{"disambiguationData":[TD([subQ4])],"derivedFrom":subQ14})]})}),makeQuery(id+"F11.opExtrude","SWEPT_FACE",FACE,{"disambiguationData":[OSD([sQuery(id+"F10.wireOp",EDGE,"E4.left")])]})]});}
            var Q22;
            {var subQ1=makeQuery(id+"F5.opExtrude","SWEPT_FACE",FACE,{"disambiguationData":[OSD([sQuery(id+"F4.wireOp",EDGE,"E2.top")])]});var subQ2=makeQuery(id+"F3.boolean.opBoolean","COPY",FACE,{"derivedFrom":makeQuery(id+"F3.opExtrude","SWEPT_FACE",FACE,{"disambiguationData":[OSD([sQuery(id+"F2.wireOp",EDGE,"E1.top")])]})});var subQ3=sQuery(id+"F0.wireOp",EDGE,"E0.left");var subQ4=makeQuery(id+"F1.opExtrude","SWEPT_FACE",FACE,{"disambiguationData":[OSD([subQ3])]});var subQ14=makeQuery(id+"F5.boolean.opBoolean","MERGE",FACE,{"derivedFrom":[subQ2,subQ1]});var subQ16=sQuery(id+"F0.wireOp",EDGE,"E0.right");var subQ17=makeQuery(id+"F1.opExtrude","SWEPT_FACE",FACE,{"disambiguationData":[OSD([subQ16])]});var subQ21=sQuery(id+"F0.wireOp",EDGE,"E0.top");var subQ22=sQuery(id+"F0.wireOp",EDGE,"E0.bottom");Q22=makeQuery(id+"F11.boolean.opBoolean","INTERSECT",EDGE,{"derivedFrom":[makeQuery(id+"F9.opFillet","SPLIT",FACE,{"disambiguationData":[OD(3.0)],"derivedFrom":makeQuery(id+"F8.opFillet","MERGE",FACE,{"derivedFrom":[makeQuery(id+"F7.boolean.opBoolean","SPLIT",FACE,{"disambiguationData":[TD([makeQuery(id+"F1.opExtrude","CAP_FACE",FACE,{"disambiguationData":[OSD([subQ22,subQ21,subQ3,subQ16])],"isStart":false})])],"derivedFrom":subQ14}),makeQuery(id+"F7.boolean.opBoolean","SPLIT",FACE,{"disambiguationData":[TD([makeQuery(id+"F1.opExtrude","CAP_FACE",FACE,{"disambiguationData":[OSD([subQ22,subQ21,subQ3,subQ16])],"isStart":true})])],"derivedFrom":subQ14}),makeQuery(id+"F7.boolean.opBoolean","SPLIT",FACE,{"disambiguationData":[TD([subQ17])],"derivedFrom":subQ14}),makeQuery(id+"F7.boolean.opBoolean","SPLIT",FACE,{"disambiguationData":[TD([subQ4])],"derivedFrom":subQ14})]})}),makeQuery(id+"F11.opExtrude","SWEPT_FACE",FACE,{"disambiguationData":[OSD([sQuery(id+"F10.wireOp",EDGE,"E8.1.2.1")])]})]});}
            var Q23;
            {var subQ1=makeQuery(id+"F5.opExtrude","SWEPT_FACE",FACE,{"disambiguationData":[OSD([sQuery(id+"F4.wireOp",EDGE,"E2.top")])]});var subQ2=makeQuery(id+"F3.boolean.opBoolean","COPY",FACE,{"derivedFrom":makeQuery(id+"F3.opExtrude","SWEPT_FACE",FACE,{"disambiguationData":[OSD([sQuery(id+"F2.wireOp",EDGE,"E1.top")])]})});var subQ3=sQuery(id+"F0.wireOp",EDGE,"E0.left");var subQ4=makeQuery(id+"F1.opExtrude","SWEPT_FACE",FACE,{"disambiguationData":[OSD([subQ3])]});var subQ14=makeQuery(id+"F5.boolean.opBoolean","MERGE",FACE,{"derivedFrom":[subQ2,subQ1]});var subQ16=sQuery(id+"F0.wireOp",EDGE,"E0.right");var subQ17=makeQuery(id+"F1.opExtrude","SWEPT_FACE",FACE,{"disambiguationData":[OSD([subQ16])]});var subQ21=sQuery(id+"F0.wireOp",EDGE,"E0.top");var subQ22=sQuery(id+"F0.wireOp",EDGE,"E0.bottom");Q23=makeQuery(id+"F11.boolean.opBoolean","INTERSECT",EDGE,{"derivedFrom":[makeQuery(id+"F9.opFillet","SPLIT",FACE,{"disambiguationData":[OD(3.0)],"derivedFrom":makeQuery(id+"F8.opFillet","MERGE",FACE,{"derivedFrom":[makeQuery(id+"F7.boolean.opBoolean","SPLIT",FACE,{"disambiguationData":[TD([makeQuery(id+"F1.opExtrude","CAP_FACE",FACE,{"disambiguationData":[OSD([subQ22,subQ21,subQ3,subQ16])],"isStart":false})])],"derivedFrom":subQ14}),makeQuery(id+"F7.boolean.opBoolean","SPLIT",FACE,{"disambiguationData":[TD([makeQuery(id+"F1.opExtrude","CAP_FACE",FACE,{"disambiguationData":[OSD([subQ22,subQ21,subQ3,subQ16])],"isStart":true})])],"derivedFrom":subQ14}),makeQuery(id+"F7.boolean.opBoolean","SPLIT",FACE,{"disambiguationData":[TD([subQ17])],"derivedFrom":subQ14}),makeQuery(id+"F7.boolean.opBoolean","SPLIT",FACE,{"disambiguationData":[TD([subQ4])],"derivedFrom":subQ14})]})}),makeQuery(id+"F11.opExtrude","SWEPT_FACE",FACE,{"disambiguationData":[OSD([sQuery(id+"F10.wireOp",EDGE,"E8.1.1.1")])]})]});}
            var Q24;
            {var subQ1=makeQuery(id+"F5.opExtrude","SWEPT_FACE",FACE,{"disambiguationData":[OSD([sQuery(id+"F4.wireOp",EDGE,"E2.top")])]});var subQ2=makeQuery(id+"F3.boolean.opBoolean","COPY",FACE,{"derivedFrom":makeQuery(id+"F3.opExtrude","SWEPT_FACE",FACE,{"disambiguationData":[OSD([sQuery(id+"F2.wireOp",EDGE,"E1.top")])]})});var subQ3=sQuery(id+"F0.wireOp",EDGE,"E0.left");var subQ4=makeQuery(id+"F1.opExtrude","SWEPT_FACE",FACE,{"disambiguationData":[OSD([subQ3])]});var subQ14=makeQuery(id+"F5.boolean.opBoolean","MERGE",FACE,{"derivedFrom":[subQ2,subQ1]});var subQ16=sQuery(id+"F0.wireOp",EDGE,"E0.right");var subQ17=makeQuery(id+"F1.opExtrude","SWEPT_FACE",FACE,{"disambiguationData":[OSD([subQ16])]});var subQ21=sQuery(id+"F0.wireOp",EDGE,"E0.top");var subQ22=sQuery(id+"F0.wireOp",EDGE,"E0.bottom");Q24=makeQuery(id+"F11.boolean.opBoolean","INTERSECT",EDGE,{"derivedFrom":[makeQuery(id+"F9.opFillet","SPLIT",FACE,{"disambiguationData":[OD(3.0)],"derivedFrom":makeQuery(id+"F8.opFillet","MERGE",FACE,{"derivedFrom":[makeQuery(id+"F7.boolean.opBoolean","SPLIT",FACE,{"disambiguationData":[TD([makeQuery(id+"F1.opExtrude","CAP_FACE",FACE,{"disambiguationData":[OSD([subQ22,subQ21,subQ3,subQ16])],"isStart":false})])],"derivedFrom":subQ14}),makeQuery(id+"F7.boolean.opBoolean","SPLIT",FACE,{"disambiguationData":[TD([makeQuery(id+"F1.opExtrude","CAP_FACE",FACE,{"disambiguationData":[OSD([subQ22,subQ21,subQ3,subQ16])],"isStart":true})])],"derivedFrom":subQ14}),makeQuery(id+"F7.boolean.opBoolean","SPLIT",FACE,{"disambiguationData":[TD([subQ17])],"derivedFrom":subQ14}),makeQuery(id+"F7.boolean.opBoolean","SPLIT",FACE,{"disambiguationData":[TD([subQ4])],"derivedFrom":subQ14})]})}),makeQuery(id+"F11.opExtrude","SWEPT_FACE",FACE,{"disambiguationData":[OSD([sQuery(id+"F10.wireOp",EDGE,"E8.1.0.1")])]})]});}
            var Q25;
            {var subQ0=makeQuery(id+"F5.opExtrude","SWEPT_FACE",FACE,{"disambiguationData":[OSD([sQuery(id+"F4.wireOp",EDGE,"E2.bottom")])]});var subQ2=makeQuery(id+"F3.boolean.opBoolean","COPY",FACE,{"derivedFrom":makeQuery(id+"F3.opExtrude","SWEPT_FACE",FACE,{"disambiguationData":[OSD([sQuery(id+"F2.wireOp",EDGE,"E1.bottom")])]})});var subQ3=sQuery(id+"F0.wireOp",EDGE,"E0.left");var subQ4=makeQuery(id+"F1.opExtrude","SWEPT_FACE",FACE,{"disambiguationData":[OSD([subQ3])]});var subQ14=makeQuery(id+"F5.boolean.opBoolean","MERGE",FACE,{"derivedFrom":[subQ2,subQ0]});var subQ16=sQuery(id+"F0.wireOp",EDGE,"E0.right");var subQ17=makeQuery(id+"F1.opExtrude","SWEPT_FACE",FACE,{"disambiguationData":[OSD([subQ16])]});var subQ21=sQuery(id+"F0.wireOp",EDGE,"E0.top");var subQ22=sQuery(id+"F0.wireOp",EDGE,"E0.bottom");Q25=makeQuery(id+"F11.boolean.opBoolean","INTERSECT",EDGE,{"derivedFrom":[makeQuery(id+"F9.opFillet","SPLIT",FACE,{"disambiguationData":[OD(3.0)],"derivedFrom":makeQuery(id+"F8.opFillet","MERGE",FACE,{"derivedFrom":[makeQuery(id+"F7.boolean.opBoolean","SPLIT",FACE,{"disambiguationData":[TD([makeQuery(id+"F1.opExtrude","CAP_FACE",FACE,{"disambiguationData":[OSD([subQ22,subQ21,subQ3,subQ16])],"isStart":false})])],"derivedFrom":subQ14}),makeQuery(id+"F7.boolean.opBoolean","SPLIT",FACE,{"disambiguationData":[TD([makeQuery(id+"F1.opExtrude","CAP_FACE",FACE,{"disambiguationData":[OSD([subQ22,subQ21,subQ3,subQ16])],"isStart":true})])],"derivedFrom":subQ14}),makeQuery(id+"F7.boolean.opBoolean","SPLIT",FACE,{"disambiguationData":[TD([subQ17])],"derivedFrom":subQ14}),makeQuery(id+"F7.boolean.opBoolean","SPLIT",FACE,{"disambiguationData":[TD([subQ4])],"derivedFrom":subQ14})]})}),makeQuery(id+"F11.opExtrude","SWEPT_FACE",FACE,{"disambiguationData":[OSD([sQuery(id+"F10.wireOp",EDGE,"E8.1.0.1")])]})]});}
            var Q26;
            {var subQ0=makeQuery(id+"F5.opExtrude","SWEPT_FACE",FACE,{"disambiguationData":[OSD([sQuery(id+"F4.wireOp",EDGE,"E2.bottom")])]});var subQ2=makeQuery(id+"F3.boolean.opBoolean","COPY",FACE,{"derivedFrom":makeQuery(id+"F3.opExtrude","SWEPT_FACE",FACE,{"disambiguationData":[OSD([sQuery(id+"F2.wireOp",EDGE,"E1.bottom")])]})});var subQ3=sQuery(id+"F0.wireOp",EDGE,"E0.left");var subQ4=makeQuery(id+"F1.opExtrude","SWEPT_FACE",FACE,{"disambiguationData":[OSD([subQ3])]});var subQ14=makeQuery(id+"F5.boolean.opBoolean","MERGE",FACE,{"derivedFrom":[subQ2,subQ0]});var subQ16=sQuery(id+"F0.wireOp",EDGE,"E0.right");var subQ17=makeQuery(id+"F1.opExtrude","SWEPT_FACE",FACE,{"disambiguationData":[OSD([subQ16])]});var subQ21=sQuery(id+"F0.wireOp",EDGE,"E0.top");var subQ22=sQuery(id+"F0.wireOp",EDGE,"E0.bottom");Q26=makeQuery(id+"F11.boolean.opBoolean","INTERSECT",EDGE,{"derivedFrom":[makeQuery(id+"F9.opFillet","SPLIT",FACE,{"disambiguationData":[OD(3.0)],"derivedFrom":makeQuery(id+"F8.opFillet","MERGE",FACE,{"derivedFrom":[makeQuery(id+"F7.boolean.opBoolean","SPLIT",FACE,{"disambiguationData":[TD([makeQuery(id+"F1.opExtrude","CAP_FACE",FACE,{"disambiguationData":[OSD([subQ22,subQ21,subQ3,subQ16])],"isStart":false})])],"derivedFrom":subQ14}),makeQuery(id+"F7.boolean.opBoolean","SPLIT",FACE,{"disambiguationData":[TD([makeQuery(id+"F1.opExtrude","CAP_FACE",FACE,{"disambiguationData":[OSD([subQ22,subQ21,subQ3,subQ16])],"isStart":true})])],"derivedFrom":subQ14}),makeQuery(id+"F7.boolean.opBoolean","SPLIT",FACE,{"disambiguationData":[TD([subQ17])],"derivedFrom":subQ14}),makeQuery(id+"F7.boolean.opBoolean","SPLIT",FACE,{"disambiguationData":[TD([subQ4])],"derivedFrom":subQ14})]})}),makeQuery(id+"F11.opExtrude","SWEPT_FACE",FACE,{"disambiguationData":[OSD([sQuery(id+"F10.wireOp",EDGE,"E8.1.1.1")])]})]});}
            var Q27;
            {var subQ0=makeQuery(id+"F5.opExtrude","SWEPT_FACE",FACE,{"disambiguationData":[OSD([sQuery(id+"F4.wireOp",EDGE,"E2.bottom")])]});var subQ2=makeQuery(id+"F3.boolean.opBoolean","COPY",FACE,{"derivedFrom":makeQuery(id+"F3.opExtrude","SWEPT_FACE",FACE,{"disambiguationData":[OSD([sQuery(id+"F2.wireOp",EDGE,"E1.bottom")])]})});var subQ3=sQuery(id+"F0.wireOp",EDGE,"E0.left");var subQ4=makeQuery(id+"F1.opExtrude","SWEPT_FACE",FACE,{"disambiguationData":[OSD([subQ3])]});var subQ14=makeQuery(id+"F5.boolean.opBoolean","MERGE",FACE,{"derivedFrom":[subQ2,subQ0]});var subQ16=sQuery(id+"F0.wireOp",EDGE,"E0.right");var subQ17=makeQuery(id+"F1.opExtrude","SWEPT_FACE",FACE,{"disambiguationData":[OSD([subQ16])]});var subQ21=sQuery(id+"F0.wireOp",EDGE,"E0.top");var subQ22=sQuery(id+"F0.wireOp",EDGE,"E0.bottom");Q27=makeQuery(id+"F11.boolean.opBoolean","INTERSECT",EDGE,{"derivedFrom":[makeQuery(id+"F9.opFillet","SPLIT",FACE,{"disambiguationData":[OD(3.0)],"derivedFrom":makeQuery(id+"F8.opFillet","MERGE",FACE,{"derivedFrom":[makeQuery(id+"F7.boolean.opBoolean","SPLIT",FACE,{"disambiguationData":[TD([makeQuery(id+"F1.opExtrude","CAP_FACE",FACE,{"disambiguationData":[OSD([subQ22,subQ21,subQ3,subQ16])],"isStart":false})])],"derivedFrom":subQ14}),makeQuery(id+"F7.boolean.opBoolean","SPLIT",FACE,{"disambiguationData":[TD([makeQuery(id+"F1.opExtrude","CAP_FACE",FACE,{"disambiguationData":[OSD([subQ22,subQ21,subQ3,subQ16])],"isStart":true})])],"derivedFrom":subQ14}),makeQuery(id+"F7.boolean.opBoolean","SPLIT",FACE,{"disambiguationData":[TD([subQ17])],"derivedFrom":subQ14}),makeQuery(id+"F7.boolean.opBoolean","SPLIT",FACE,{"disambiguationData":[TD([subQ4])],"derivedFrom":subQ14})]})}),makeQuery(id+"F11.opExtrude","SWEPT_FACE",FACE,{"disambiguationData":[OSD([sQuery(id+"F10.wireOp",EDGE,"E8.1.2.1")])]})]});}
            var Q28;
            {var subQ0=makeQuery(id+"F5.opExtrude","SWEPT_FACE",FACE,{"disambiguationData":[OSD([sQuery(id+"F4.wireOp",EDGE,"E2.bottom")])]});var subQ2=makeQuery(id+"F3.boolean.opBoolean","COPY",FACE,{"derivedFrom":makeQuery(id+"F3.opExtrude","SWEPT_FACE",FACE,{"disambiguationData":[OSD([sQuery(id+"F2.wireOp",EDGE,"E1.bottom")])]})});var subQ3=sQuery(id+"F0.wireOp",EDGE,"E0.left");var subQ4=makeQuery(id+"F1.opExtrude","SWEPT_FACE",FACE,{"disambiguationData":[OSD([subQ3])]});var subQ14=makeQuery(id+"F5.boolean.opBoolean","MERGE",FACE,{"derivedFrom":[subQ2,subQ0]});var subQ16=sQuery(id+"F0.wireOp",EDGE,"E0.right");var subQ17=makeQuery(id+"F1.opExtrude","SWEPT_FACE",FACE,{"disambiguationData":[OSD([subQ16])]});var subQ21=sQuery(id+"F0.wireOp",EDGE,"E0.top");var subQ22=sQuery(id+"F0.wireOp",EDGE,"E0.bottom");Q28=makeQuery(id+"F11.boolean.opBoolean","INTERSECT",EDGE,{"derivedFrom":[makeQuery(id+"F9.opFillet","SPLIT",FACE,{"disambiguationData":[OD(1.0)],"derivedFrom":makeQuery(id+"F8.opFillet","MERGE",FACE,{"derivedFrom":[makeQuery(id+"F7.boolean.opBoolean","SPLIT",FACE,{"disambiguationData":[TD([makeQuery(id+"F1.opExtrude","CAP_FACE",FACE,{"disambiguationData":[OSD([subQ22,subQ21,subQ3,subQ16])],"isStart":false})])],"derivedFrom":subQ14}),makeQuery(id+"F7.boolean.opBoolean","SPLIT",FACE,{"disambiguationData":[TD([makeQuery(id+"F1.opExtrude","CAP_FACE",FACE,{"disambiguationData":[OSD([subQ22,subQ21,subQ3,subQ16])],"isStart":true})])],"derivedFrom":subQ14}),makeQuery(id+"F7.boolean.opBoolean","SPLIT",FACE,{"disambiguationData":[TD([subQ17])],"derivedFrom":subQ14}),makeQuery(id+"F7.boolean.opBoolean","SPLIT",FACE,{"disambiguationData":[TD([subQ4])],"derivedFrom":subQ14})]})}),makeQuery(id+"F11.opExtrude","SWEPT_FACE",FACE,{"disambiguationData":[OSD([sQuery(id+"F10.wireOp",EDGE,"E6.0.1.2")])]})]});}
            var Q29;
            {var subQ0=makeQuery(id+"F5.opExtrude","SWEPT_FACE",FACE,{"disambiguationData":[OSD([sQuery(id+"F4.wireOp",EDGE,"E2.bottom")])]});var subQ2=makeQuery(id+"F3.boolean.opBoolean","COPY",FACE,{"derivedFrom":makeQuery(id+"F3.opExtrude","SWEPT_FACE",FACE,{"disambiguationData":[OSD([sQuery(id+"F2.wireOp",EDGE,"E1.bottom")])]})});var subQ3=sQuery(id+"F0.wireOp",EDGE,"E0.left");var subQ4=makeQuery(id+"F1.opExtrude","SWEPT_FACE",FACE,{"disambiguationData":[OSD([subQ3])]});var subQ14=makeQuery(id+"F5.boolean.opBoolean","MERGE",FACE,{"derivedFrom":[subQ2,subQ0]});var subQ16=sQuery(id+"F0.wireOp",EDGE,"E0.right");var subQ17=makeQuery(id+"F1.opExtrude","SWEPT_FACE",FACE,{"disambiguationData":[OSD([subQ16])]});var subQ21=sQuery(id+"F0.wireOp",EDGE,"E0.top");var subQ22=sQuery(id+"F0.wireOp",EDGE,"E0.bottom");Q29=makeQuery(id+"F11.boolean.opBoolean","INTERSECT",EDGE,{"derivedFrom":[makeQuery(id+"F9.opFillet","SPLIT",FACE,{"disambiguationData":[OD(1.0)],"derivedFrom":makeQuery(id+"F8.opFillet","MERGE",FACE,{"derivedFrom":[makeQuery(id+"F7.boolean.opBoolean","SPLIT",FACE,{"disambiguationData":[TD([makeQuery(id+"F1.opExtrude","CAP_FACE",FACE,{"disambiguationData":[OSD([subQ22,subQ21,subQ3,subQ16])],"isStart":false})])],"derivedFrom":subQ14}),makeQuery(id+"F7.boolean.opBoolean","SPLIT",FACE,{"disambiguationData":[TD([makeQuery(id+"F1.opExtrude","CAP_FACE",FACE,{"disambiguationData":[OSD([subQ22,subQ21,subQ3,subQ16])],"isStart":true})])],"derivedFrom":subQ14}),makeQuery(id+"F7.boolean.opBoolean","SPLIT",FACE,{"disambiguationData":[TD([subQ17])],"derivedFrom":subQ14}),makeQuery(id+"F7.boolean.opBoolean","SPLIT",FACE,{"disambiguationData":[TD([subQ4])],"derivedFrom":subQ14})]})}),makeQuery(id+"F11.opExtrude","SWEPT_FACE",FACE,{"disambiguationData":[OSD([sQuery(id+"F10.wireOp",EDGE,"E6.0.1.14")])]})]});}
            var Q30;
            {var subQ1=makeQuery(id+"F5.opExtrude","SWEPT_FACE",FACE,{"disambiguationData":[OSD([sQuery(id+"F4.wireOp",EDGE,"E2.top")])]});var subQ2=makeQuery(id+"F3.boolean.opBoolean","COPY",FACE,{"derivedFrom":makeQuery(id+"F3.opExtrude","SWEPT_FACE",FACE,{"disambiguationData":[OSD([sQuery(id+"F2.wireOp",EDGE,"E1.top")])]})});var subQ3=sQuery(id+"F0.wireOp",EDGE,"E0.left");var subQ4=makeQuery(id+"F1.opExtrude","SWEPT_FACE",FACE,{"disambiguationData":[OSD([subQ3])]});var subQ14=makeQuery(id+"F5.boolean.opBoolean","MERGE",FACE,{"derivedFrom":[subQ2,subQ1]});var subQ16=sQuery(id+"F0.wireOp",EDGE,"E0.right");var subQ17=makeQuery(id+"F1.opExtrude","SWEPT_FACE",FACE,{"disambiguationData":[OSD([subQ16])]});var subQ21=sQuery(id+"F0.wireOp",EDGE,"E0.top");var subQ22=sQuery(id+"F0.wireOp",EDGE,"E0.bottom");Q30=makeQuery(id+"F11.boolean.opBoolean","INTERSECT",EDGE,{"derivedFrom":[makeQuery(id+"F9.opFillet","SPLIT",FACE,{"disambiguationData":[OD(3.0)],"derivedFrom":makeQuery(id+"F8.opFillet","MERGE",FACE,{"derivedFrom":[makeQuery(id+"F7.boolean.opBoolean","SPLIT",FACE,{"disambiguationData":[TD([makeQuery(id+"F1.opExtrude","CAP_FACE",FACE,{"disambiguationData":[OSD([subQ22,subQ21,subQ3,subQ16])],"isStart":false})])],"derivedFrom":subQ14}),makeQuery(id+"F7.boolean.opBoolean","SPLIT",FACE,{"disambiguationData":[TD([makeQuery(id+"F1.opExtrude","CAP_FACE",FACE,{"disambiguationData":[OSD([subQ22,subQ21,subQ3,subQ16])],"isStart":true})])],"derivedFrom":subQ14}),makeQuery(id+"F7.boolean.opBoolean","SPLIT",FACE,{"disambiguationData":[TD([subQ17])],"derivedFrom":subQ14}),makeQuery(id+"F7.boolean.opBoolean","SPLIT",FACE,{"disambiguationData":[TD([subQ4])],"derivedFrom":subQ14})]})}),makeQuery(id+"F11.opExtrude","SWEPT_FACE",FACE,{"disambiguationData":[OSD([sQuery(id+"F10.wireOp",EDGE,"E8.1.2.0")])]})]});}
            var Q31;
            {var subQ1=makeQuery(id+"F5.opExtrude","SWEPT_FACE",FACE,{"disambiguationData":[OSD([sQuery(id+"F4.wireOp",EDGE,"E2.top")])]});var subQ2=makeQuery(id+"F3.boolean.opBoolean","COPY",FACE,{"derivedFrom":makeQuery(id+"F3.opExtrude","SWEPT_FACE",FACE,{"disambiguationData":[OSD([sQuery(id+"F2.wireOp",EDGE,"E1.top")])]})});var subQ3=sQuery(id+"F0.wireOp",EDGE,"E0.left");var subQ4=makeQuery(id+"F1.opExtrude","SWEPT_FACE",FACE,{"disambiguationData":[OSD([subQ3])]});var subQ14=makeQuery(id+"F5.boolean.opBoolean","MERGE",FACE,{"derivedFrom":[subQ2,subQ1]});var subQ16=sQuery(id+"F0.wireOp",EDGE,"E0.right");var subQ17=makeQuery(id+"F1.opExtrude","SWEPT_FACE",FACE,{"disambiguationData":[OSD([subQ16])]});var subQ21=sQuery(id+"F0.wireOp",EDGE,"E0.top");var subQ22=sQuery(id+"F0.wireOp",EDGE,"E0.bottom");Q31=makeQuery(id+"F11.boolean.opBoolean","INTERSECT",EDGE,{"derivedFrom":[makeQuery(id+"F9.opFillet","SPLIT",FACE,{"disambiguationData":[OD(3.0)],"derivedFrom":makeQuery(id+"F8.opFillet","MERGE",FACE,{"derivedFrom":[makeQuery(id+"F7.boolean.opBoolean","SPLIT",FACE,{"disambiguationData":[TD([makeQuery(id+"F1.opExtrude","CAP_FACE",FACE,{"disambiguationData":[OSD([subQ22,subQ21,subQ3,subQ16])],"isStart":false})])],"derivedFrom":subQ14}),makeQuery(id+"F7.boolean.opBoolean","SPLIT",FACE,{"disambiguationData":[TD([makeQuery(id+"F1.opExtrude","CAP_FACE",FACE,{"disambiguationData":[OSD([subQ22,subQ21,subQ3,subQ16])],"isStart":true})])],"derivedFrom":subQ14}),makeQuery(id+"F7.boolean.opBoolean","SPLIT",FACE,{"disambiguationData":[TD([subQ17])],"derivedFrom":subQ14}),makeQuery(id+"F7.boolean.opBoolean","SPLIT",FACE,{"disambiguationData":[TD([subQ4])],"derivedFrom":subQ14})]})}),makeQuery(id+"F11.opExtrude","SWEPT_FACE",FACE,{"disambiguationData":[OSD([sQuery(id+"F10.wireOp",EDGE,"E8.1.1.0")])]})]});}
            var Q32;
            {var subQ1=makeQuery(id+"F5.opExtrude","SWEPT_FACE",FACE,{"disambiguationData":[OSD([sQuery(id+"F4.wireOp",EDGE,"E2.top")])]});var subQ2=makeQuery(id+"F3.boolean.opBoolean","COPY",FACE,{"derivedFrom":makeQuery(id+"F3.opExtrude","SWEPT_FACE",FACE,{"disambiguationData":[OSD([sQuery(id+"F2.wireOp",EDGE,"E1.top")])]})});var subQ3=sQuery(id+"F0.wireOp",EDGE,"E0.left");var subQ4=makeQuery(id+"F1.opExtrude","SWEPT_FACE",FACE,{"disambiguationData":[OSD([subQ3])]});var subQ14=makeQuery(id+"F5.boolean.opBoolean","MERGE",FACE,{"derivedFrom":[subQ2,subQ1]});var subQ16=sQuery(id+"F0.wireOp",EDGE,"E0.right");var subQ17=makeQuery(id+"F1.opExtrude","SWEPT_FACE",FACE,{"disambiguationData":[OSD([subQ16])]});var subQ21=sQuery(id+"F0.wireOp",EDGE,"E0.top");var subQ22=sQuery(id+"F0.wireOp",EDGE,"E0.bottom");Q32=makeQuery(id+"F11.boolean.opBoolean","INTERSECT",EDGE,{"derivedFrom":[makeQuery(id+"F9.opFillet","SPLIT",FACE,{"disambiguationData":[OD(3.0)],"derivedFrom":makeQuery(id+"F8.opFillet","MERGE",FACE,{"derivedFrom":[makeQuery(id+"F7.boolean.opBoolean","SPLIT",FACE,{"disambiguationData":[TD([makeQuery(id+"F1.opExtrude","CAP_FACE",FACE,{"disambiguationData":[OSD([subQ22,subQ21,subQ3,subQ16])],"isStart":false})])],"derivedFrom":subQ14}),makeQuery(id+"F7.boolean.opBoolean","SPLIT",FACE,{"disambiguationData":[TD([makeQuery(id+"F1.opExtrude","CAP_FACE",FACE,{"disambiguationData":[OSD([subQ22,subQ21,subQ3,subQ16])],"isStart":true})])],"derivedFrom":subQ14}),makeQuery(id+"F7.boolean.opBoolean","SPLIT",FACE,{"disambiguationData":[TD([subQ17])],"derivedFrom":subQ14}),makeQuery(id+"F7.boolean.opBoolean","SPLIT",FACE,{"disambiguationData":[TD([subQ4])],"derivedFrom":subQ14})]})}),makeQuery(id+"F11.opExtrude","SWEPT_FACE",FACE,{"disambiguationData":[OSD([sQuery(id+"F10.wireOp",EDGE,"E8.1.0.0")])]})]});}
            var Q33;
            {var subQ0=makeQuery(id+"F5.opExtrude","SWEPT_FACE",FACE,{"disambiguationData":[OSD([sQuery(id+"F4.wireOp",EDGE,"E2.bottom")])]});var subQ2=makeQuery(id+"F3.boolean.opBoolean","COPY",FACE,{"derivedFrom":makeQuery(id+"F3.opExtrude","SWEPT_FACE",FACE,{"disambiguationData":[OSD([sQuery(id+"F2.wireOp",EDGE,"E1.bottom")])]})});var subQ3=sQuery(id+"F0.wireOp",EDGE,"E0.left");var subQ4=makeQuery(id+"F1.opExtrude","SWEPT_FACE",FACE,{"disambiguationData":[OSD([subQ3])]});var subQ14=makeQuery(id+"F5.boolean.opBoolean","MERGE",FACE,{"derivedFrom":[subQ2,subQ0]});var subQ16=sQuery(id+"F0.wireOp",EDGE,"E0.right");var subQ17=makeQuery(id+"F1.opExtrude","SWEPT_FACE",FACE,{"disambiguationData":[OSD([subQ16])]});var subQ21=sQuery(id+"F0.wireOp",EDGE,"E0.top");var subQ22=sQuery(id+"F0.wireOp",EDGE,"E0.bottom");Q33=makeQuery(id+"F11.boolean.opBoolean","INTERSECT",EDGE,{"derivedFrom":[makeQuery(id+"F9.opFillet","SPLIT",FACE,{"disambiguationData":[OD(3.0)],"derivedFrom":makeQuery(id+"F8.opFillet","MERGE",FACE,{"derivedFrom":[makeQuery(id+"F7.boolean.opBoolean","SPLIT",FACE,{"disambiguationData":[TD([makeQuery(id+"F1.opExtrude","CAP_FACE",FACE,{"disambiguationData":[OSD([subQ22,subQ21,subQ3,subQ16])],"isStart":false})])],"derivedFrom":subQ14}),makeQuery(id+"F7.boolean.opBoolean","SPLIT",FACE,{"disambiguationData":[TD([makeQuery(id+"F1.opExtrude","CAP_FACE",FACE,{"disambiguationData":[OSD([subQ22,subQ21,subQ3,subQ16])],"isStart":true})])],"derivedFrom":subQ14}),makeQuery(id+"F7.boolean.opBoolean","SPLIT",FACE,{"disambiguationData":[TD([subQ17])],"derivedFrom":subQ14}),makeQuery(id+"F7.boolean.opBoolean","SPLIT",FACE,{"disambiguationData":[TD([subQ4])],"derivedFrom":subQ14})]})}),makeQuery(id+"F11.opExtrude","SWEPT_FACE",FACE,{"disambiguationData":[OSD([sQuery(id+"F10.wireOp",EDGE,"E8.1.0.0")])]})]});}
            var Q34;
            {var subQ0=makeQuery(id+"F5.opExtrude","SWEPT_FACE",FACE,{"disambiguationData":[OSD([sQuery(id+"F4.wireOp",EDGE,"E2.bottom")])]});var subQ2=makeQuery(id+"F3.boolean.opBoolean","COPY",FACE,{"derivedFrom":makeQuery(id+"F3.opExtrude","SWEPT_FACE",FACE,{"disambiguationData":[OSD([sQuery(id+"F2.wireOp",EDGE,"E1.bottom")])]})});var subQ3=sQuery(id+"F0.wireOp",EDGE,"E0.left");var subQ4=makeQuery(id+"F1.opExtrude","SWEPT_FACE",FACE,{"disambiguationData":[OSD([subQ3])]});var subQ14=makeQuery(id+"F5.boolean.opBoolean","MERGE",FACE,{"derivedFrom":[subQ2,subQ0]});var subQ16=sQuery(id+"F0.wireOp",EDGE,"E0.right");var subQ17=makeQuery(id+"F1.opExtrude","SWEPT_FACE",FACE,{"disambiguationData":[OSD([subQ16])]});var subQ21=sQuery(id+"F0.wireOp",EDGE,"E0.top");var subQ22=sQuery(id+"F0.wireOp",EDGE,"E0.bottom");Q34=makeQuery(id+"F11.boolean.opBoolean","INTERSECT",EDGE,{"derivedFrom":[makeQuery(id+"F9.opFillet","SPLIT",FACE,{"disambiguationData":[OD(3.0)],"derivedFrom":makeQuery(id+"F8.opFillet","MERGE",FACE,{"derivedFrom":[makeQuery(id+"F7.boolean.opBoolean","SPLIT",FACE,{"disambiguationData":[TD([makeQuery(id+"F1.opExtrude","CAP_FACE",FACE,{"disambiguationData":[OSD([subQ22,subQ21,subQ3,subQ16])],"isStart":false})])],"derivedFrom":subQ14}),makeQuery(id+"F7.boolean.opBoolean","SPLIT",FACE,{"disambiguationData":[TD([makeQuery(id+"F1.opExtrude","CAP_FACE",FACE,{"disambiguationData":[OSD([subQ22,subQ21,subQ3,subQ16])],"isStart":true})])],"derivedFrom":subQ14}),makeQuery(id+"F7.boolean.opBoolean","SPLIT",FACE,{"disambiguationData":[TD([subQ17])],"derivedFrom":subQ14}),makeQuery(id+"F7.boolean.opBoolean","SPLIT",FACE,{"disambiguationData":[TD([subQ4])],"derivedFrom":subQ14})]})}),makeQuery(id+"F11.opExtrude","SWEPT_FACE",FACE,{"disambiguationData":[OSD([sQuery(id+"F10.wireOp",EDGE,"E8.1.1.0")])]})]});}
            var Q35;
            {var subQ0=makeQuery(id+"F5.opExtrude","SWEPT_FACE",FACE,{"disambiguationData":[OSD([sQuery(id+"F4.wireOp",EDGE,"E2.bottom")])]});var subQ2=makeQuery(id+"F3.boolean.opBoolean","COPY",FACE,{"derivedFrom":makeQuery(id+"F3.opExtrude","SWEPT_FACE",FACE,{"disambiguationData":[OSD([sQuery(id+"F2.wireOp",EDGE,"E1.bottom")])]})});var subQ3=sQuery(id+"F0.wireOp",EDGE,"E0.left");var subQ4=makeQuery(id+"F1.opExtrude","SWEPT_FACE",FACE,{"disambiguationData":[OSD([subQ3])]});var subQ14=makeQuery(id+"F5.boolean.opBoolean","MERGE",FACE,{"derivedFrom":[subQ2,subQ0]});var subQ16=sQuery(id+"F0.wireOp",EDGE,"E0.right");var subQ17=makeQuery(id+"F1.opExtrude","SWEPT_FACE",FACE,{"disambiguationData":[OSD([subQ16])]});var subQ21=sQuery(id+"F0.wireOp",EDGE,"E0.top");var subQ22=sQuery(id+"F0.wireOp",EDGE,"E0.bottom");Q35=makeQuery(id+"F11.boolean.opBoolean","INTERSECT",EDGE,{"derivedFrom":[makeQuery(id+"F9.opFillet","SPLIT",FACE,{"disambiguationData":[OD(3.0)],"derivedFrom":makeQuery(id+"F8.opFillet","MERGE",FACE,{"derivedFrom":[makeQuery(id+"F7.boolean.opBoolean","SPLIT",FACE,{"disambiguationData":[TD([makeQuery(id+"F1.opExtrude","CAP_FACE",FACE,{"disambiguationData":[OSD([subQ22,subQ21,subQ3,subQ16])],"isStart":false})])],"derivedFrom":subQ14}),makeQuery(id+"F7.boolean.opBoolean","SPLIT",FACE,{"disambiguationData":[TD([makeQuery(id+"F1.opExtrude","CAP_FACE",FACE,{"disambiguationData":[OSD([subQ22,subQ21,subQ3,subQ16])],"isStart":true})])],"derivedFrom":subQ14}),makeQuery(id+"F7.boolean.opBoolean","SPLIT",FACE,{"disambiguationData":[TD([subQ17])],"derivedFrom":subQ14}),makeQuery(id+"F7.boolean.opBoolean","SPLIT",FACE,{"disambiguationData":[TD([subQ4])],"derivedFrom":subQ14})]})}),makeQuery(id+"F11.opExtrude","SWEPT_FACE",FACE,{"disambiguationData":[OSD([sQuery(id+"F10.wireOp",EDGE,"E8.1.2.0")])]})]});}
            var Q36;
            {var subQ0=makeQuery(id+"F5.opExtrude","SWEPT_FACE",FACE,{"disambiguationData":[OSD([sQuery(id+"F4.wireOp",EDGE,"E2.bottom")])]});var subQ2=makeQuery(id+"F3.boolean.opBoolean","COPY",FACE,{"derivedFrom":makeQuery(id+"F3.opExtrude","SWEPT_FACE",FACE,{"disambiguationData":[OSD([sQuery(id+"F2.wireOp",EDGE,"E1.bottom")])]})});var subQ3=sQuery(id+"F0.wireOp",EDGE,"E0.left");var subQ4=makeQuery(id+"F1.opExtrude","SWEPT_FACE",FACE,{"disambiguationData":[OSD([subQ3])]});var subQ14=makeQuery(id+"F5.boolean.opBoolean","MERGE",FACE,{"derivedFrom":[subQ2,subQ0]});var subQ16=sQuery(id+"F0.wireOp",EDGE,"E0.right");var subQ17=makeQuery(id+"F1.opExtrude","SWEPT_FACE",FACE,{"disambiguationData":[OSD([subQ16])]});var subQ21=sQuery(id+"F0.wireOp",EDGE,"E0.top");var subQ22=sQuery(id+"F0.wireOp",EDGE,"E0.bottom");Q36=makeQuery(id+"F11.boolean.opBoolean","INTERSECT",EDGE,{"derivedFrom":[makeQuery(id+"F9.opFillet","SPLIT",FACE,{"disambiguationData":[OD(1.0)],"derivedFrom":makeQuery(id+"F8.opFillet","MERGE",FACE,{"derivedFrom":[makeQuery(id+"F7.boolean.opBoolean","SPLIT",FACE,{"disambiguationData":[TD([makeQuery(id+"F1.opExtrude","CAP_FACE",FACE,{"disambiguationData":[OSD([subQ22,subQ21,subQ3,subQ16])],"isStart":false})])],"derivedFrom":subQ14}),makeQuery(id+"F7.boolean.opBoolean","SPLIT",FACE,{"disambiguationData":[TD([makeQuery(id+"F1.opExtrude","CAP_FACE",FACE,{"disambiguationData":[OSD([subQ22,subQ21,subQ3,subQ16])],"isStart":true})])],"derivedFrom":subQ14}),makeQuery(id+"F7.boolean.opBoolean","SPLIT",FACE,{"disambiguationData":[TD([subQ17])],"derivedFrom":subQ14}),makeQuery(id+"F7.boolean.opBoolean","SPLIT",FACE,{"disambiguationData":[TD([subQ4])],"derivedFrom":subQ14})]})}),makeQuery(id+"F11.opExtrude","SWEPT_FACE",FACE,{"disambiguationData":[OSD([sQuery(id+"F10.wireOp",EDGE,"E6.0.1.16")])]})]});}
            var Q37;
            {var subQ1=makeQuery(id+"F5.opExtrude","SWEPT_FACE",FACE,{"disambiguationData":[OSD([sQuery(id+"F4.wireOp",EDGE,"E2.top")])]});var subQ2=makeQuery(id+"F3.boolean.opBoolean","COPY",FACE,{"derivedFrom":makeQuery(id+"F3.opExtrude","SWEPT_FACE",FACE,{"disambiguationData":[OSD([sQuery(id+"F2.wireOp",EDGE,"E1.top")])]})});var subQ3=sQuery(id+"F0.wireOp",EDGE,"E0.left");var subQ4=makeQuery(id+"F1.opExtrude","SWEPT_FACE",FACE,{"disambiguationData":[OSD([subQ3])]});var subQ14=makeQuery(id+"F5.boolean.opBoolean","MERGE",FACE,{"derivedFrom":[subQ2,subQ1]});var subQ16=sQuery(id+"F0.wireOp",EDGE,"E0.right");var subQ17=makeQuery(id+"F1.opExtrude","SWEPT_FACE",FACE,{"disambiguationData":[OSD([subQ16])]});var subQ21=sQuery(id+"F0.wireOp",EDGE,"E0.top");var subQ22=sQuery(id+"F0.wireOp",EDGE,"E0.bottom");Q37=makeQuery(id+"F11.boolean.opBoolean","INTERSECT",EDGE,{"derivedFrom":[makeQuery(id+"F9.opFillet","SPLIT",FACE,{"disambiguationData":[OD(1.0)],"derivedFrom":makeQuery(id+"F8.opFillet","MERGE",FACE,{"derivedFrom":[makeQuery(id+"F7.boolean.opBoolean","SPLIT",FACE,{"disambiguationData":[TD([makeQuery(id+"F1.opExtrude","CAP_FACE",FACE,{"disambiguationData":[OSD([subQ22,subQ21,subQ3,subQ16])],"isStart":false})])],"derivedFrom":subQ14}),makeQuery(id+"F7.boolean.opBoolean","SPLIT",FACE,{"disambiguationData":[TD([makeQuery(id+"F1.opExtrude","CAP_FACE",FACE,{"disambiguationData":[OSD([subQ22,subQ21,subQ3,subQ16])],"isStart":true})])],"derivedFrom":subQ14}),makeQuery(id+"F7.boolean.opBoolean","SPLIT",FACE,{"disambiguationData":[TD([subQ17])],"derivedFrom":subQ14}),makeQuery(id+"F7.boolean.opBoolean","SPLIT",FACE,{"disambiguationData":[TD([subQ4])],"derivedFrom":subQ14})]})}),makeQuery(id+"F11.opExtrude","SWEPT_FACE",FACE,{"disambiguationData":[OSD([sQuery(id+"F10.wireOp",EDGE,"E6.0.1.16")])]})]});}
            var Q38;
            {var subQ1=makeQuery(id+"F5.opExtrude","SWEPT_FACE",FACE,{"disambiguationData":[OSD([sQuery(id+"F4.wireOp",EDGE,"E2.top")])]});var subQ2=makeQuery(id+"F3.boolean.opBoolean","COPY",FACE,{"derivedFrom":makeQuery(id+"F3.opExtrude","SWEPT_FACE",FACE,{"disambiguationData":[OSD([sQuery(id+"F2.wireOp",EDGE,"E1.top")])]})});var subQ3=sQuery(id+"F0.wireOp",EDGE,"E0.left");var subQ4=makeQuery(id+"F1.opExtrude","SWEPT_FACE",FACE,{"disambiguationData":[OSD([subQ3])]});var subQ14=makeQuery(id+"F5.boolean.opBoolean","MERGE",FACE,{"derivedFrom":[subQ2,subQ1]});var subQ16=sQuery(id+"F0.wireOp",EDGE,"E0.right");var subQ17=makeQuery(id+"F1.opExtrude","SWEPT_FACE",FACE,{"disambiguationData":[OSD([subQ16])]});var subQ21=sQuery(id+"F0.wireOp",EDGE,"E0.top");var subQ22=sQuery(id+"F0.wireOp",EDGE,"E0.bottom");Q38=makeQuery(id+"F11.boolean.opBoolean","INTERSECT",EDGE,{"derivedFrom":[makeQuery(id+"F9.opFillet","SPLIT",FACE,{"disambiguationData":[OD(1.0)],"derivedFrom":makeQuery(id+"F8.opFillet","MERGE",FACE,{"derivedFrom":[makeQuery(id+"F7.boolean.opBoolean","SPLIT",FACE,{"disambiguationData":[TD([makeQuery(id+"F1.opExtrude","CAP_FACE",FACE,{"disambiguationData":[OSD([subQ22,subQ21,subQ3,subQ16])],"isStart":false})])],"derivedFrom":subQ14}),makeQuery(id+"F7.boolean.opBoolean","SPLIT",FACE,{"disambiguationData":[TD([makeQuery(id+"F1.opExtrude","CAP_FACE",FACE,{"disambiguationData":[OSD([subQ22,subQ21,subQ3,subQ16])],"isStart":true})])],"derivedFrom":subQ14}),makeQuery(id+"F7.boolean.opBoolean","SPLIT",FACE,{"disambiguationData":[TD([subQ17])],"derivedFrom":subQ14}),makeQuery(id+"F7.boolean.opBoolean","SPLIT",FACE,{"disambiguationData":[TD([subQ4])],"derivedFrom":subQ14})]})}),makeQuery(id+"F11.opExtrude","SWEPT_FACE",FACE,{"disambiguationData":[OSD([sQuery(id+"F10.wireOp",EDGE,"E6.0.1.14")])]})]});}
            var Q39;
            {var subQ1=makeQuery(id+"F5.opExtrude","SWEPT_FACE",FACE,{"disambiguationData":[OSD([sQuery(id+"F4.wireOp",EDGE,"E2.top")])]});var subQ2=makeQuery(id+"F3.boolean.opBoolean","COPY",FACE,{"derivedFrom":makeQuery(id+"F3.opExtrude","SWEPT_FACE",FACE,{"disambiguationData":[OSD([sQuery(id+"F2.wireOp",EDGE,"E1.top")])]})});var subQ3=sQuery(id+"F0.wireOp",EDGE,"E0.left");var subQ4=makeQuery(id+"F1.opExtrude","SWEPT_FACE",FACE,{"disambiguationData":[OSD([subQ3])]});var subQ14=makeQuery(id+"F5.boolean.opBoolean","MERGE",FACE,{"derivedFrom":[subQ2,subQ1]});var subQ16=sQuery(id+"F0.wireOp",EDGE,"E0.right");var subQ17=makeQuery(id+"F1.opExtrude","SWEPT_FACE",FACE,{"disambiguationData":[OSD([subQ16])]});var subQ21=sQuery(id+"F0.wireOp",EDGE,"E0.top");var subQ22=sQuery(id+"F0.wireOp",EDGE,"E0.bottom");Q39=makeQuery(id+"F11.boolean.opBoolean","INTERSECT",EDGE,{"derivedFrom":[makeQuery(id+"F9.opFillet","SPLIT",FACE,{"disambiguationData":[OD(1.0)],"derivedFrom":makeQuery(id+"F8.opFillet","MERGE",FACE,{"derivedFrom":[makeQuery(id+"F7.boolean.opBoolean","SPLIT",FACE,{"disambiguationData":[TD([makeQuery(id+"F1.opExtrude","CAP_FACE",FACE,{"disambiguationData":[OSD([subQ22,subQ21,subQ3,subQ16])],"isStart":false})])],"derivedFrom":subQ14}),makeQuery(id+"F7.boolean.opBoolean","SPLIT",FACE,{"disambiguationData":[TD([makeQuery(id+"F1.opExtrude","CAP_FACE",FACE,{"disambiguationData":[OSD([subQ22,subQ21,subQ3,subQ16])],"isStart":true})])],"derivedFrom":subQ14}),makeQuery(id+"F7.boolean.opBoolean","SPLIT",FACE,{"disambiguationData":[TD([subQ17])],"derivedFrom":subQ14}),makeQuery(id+"F7.boolean.opBoolean","SPLIT",FACE,{"disambiguationData":[TD([subQ4])],"derivedFrom":subQ14})]})}),makeQuery(id+"F11.opExtrude","SWEPT_FACE",FACE,{"disambiguationData":[OSD([sQuery(id+"F10.wireOp",EDGE,"E6.0.1.2")])]})]});}
            var Q40;
            {var subQ0=makeQuery(id+"F5.opExtrude","SWEPT_FACE",FACE,{"disambiguationData":[OSD([sQuery(id+"F4.wireOp",EDGE,"E2.bottom")])]});var subQ2=makeQuery(id+"F3.boolean.opBoolean","COPY",FACE,{"derivedFrom":makeQuery(id+"F3.opExtrude","SWEPT_FACE",FACE,{"disambiguationData":[OSD([sQuery(id+"F2.wireOp",EDGE,"E1.bottom")])]})});var subQ3=sQuery(id+"F0.wireOp",EDGE,"E0.left");var subQ4=makeQuery(id+"F1.opExtrude","SWEPT_FACE",FACE,{"disambiguationData":[OSD([subQ3])]});var subQ14=makeQuery(id+"F5.boolean.opBoolean","MERGE",FACE,{"derivedFrom":[subQ2,subQ0]});var subQ16=sQuery(id+"F0.wireOp",EDGE,"E0.right");var subQ17=makeQuery(id+"F1.opExtrude","SWEPT_FACE",FACE,{"disambiguationData":[OSD([subQ16])]});var subQ21=sQuery(id+"F0.wireOp",EDGE,"E0.top");var subQ22=sQuery(id+"F0.wireOp",EDGE,"E0.bottom");Q40=makeQuery(id+"F11.boolean.opBoolean","INTERSECT",EDGE,{"derivedFrom":[makeQuery(id+"F9.opFillet","SPLIT",FACE,{"disambiguationData":[OD(1.0)],"derivedFrom":makeQuery(id+"F8.opFillet","MERGE",FACE,{"derivedFrom":[makeQuery(id+"F7.boolean.opBoolean","SPLIT",FACE,{"disambiguationData":[TD([makeQuery(id+"F1.opExtrude","CAP_FACE",FACE,{"disambiguationData":[OSD([subQ22,subQ21,subQ3,subQ16])],"isStart":false})])],"derivedFrom":subQ14}),makeQuery(id+"F7.boolean.opBoolean","SPLIT",FACE,{"disambiguationData":[TD([makeQuery(id+"F1.opExtrude","CAP_FACE",FACE,{"disambiguationData":[OSD([subQ22,subQ21,subQ3,subQ16])],"isStart":true})])],"derivedFrom":subQ14}),makeQuery(id+"F7.boolean.opBoolean","SPLIT",FACE,{"disambiguationData":[TD([subQ17])],"derivedFrom":subQ14}),makeQuery(id+"F7.boolean.opBoolean","SPLIT",FACE,{"disambiguationData":[TD([subQ4])],"derivedFrom":subQ14})]})}),makeQuery(id+"F11.opExtrude","SWEPT_FACE",FACE,{"disambiguationData":[OSD([sQuery(id+"F10.wireOp",EDGE,"E6.0.1.3")])]})]});}
            var Q41;
            {var subQ1=makeQuery(id+"F5.opExtrude","SWEPT_FACE",FACE,{"disambiguationData":[OSD([sQuery(id+"F4.wireOp",EDGE,"E2.top")])]});var subQ2=makeQuery(id+"F3.boolean.opBoolean","COPY",FACE,{"derivedFrom":makeQuery(id+"F3.opExtrude","SWEPT_FACE",FACE,{"disambiguationData":[OSD([sQuery(id+"F2.wireOp",EDGE,"E1.top")])]})});var subQ3=sQuery(id+"F0.wireOp",EDGE,"E0.left");var subQ4=makeQuery(id+"F1.opExtrude","SWEPT_FACE",FACE,{"disambiguationData":[OSD([subQ3])]});var subQ14=makeQuery(id+"F5.boolean.opBoolean","MERGE",FACE,{"derivedFrom":[subQ2,subQ1]});var subQ16=sQuery(id+"F0.wireOp",EDGE,"E0.right");var subQ17=makeQuery(id+"F1.opExtrude","SWEPT_FACE",FACE,{"disambiguationData":[OSD([subQ16])]});var subQ21=sQuery(id+"F0.wireOp",EDGE,"E0.top");var subQ22=sQuery(id+"F0.wireOp",EDGE,"E0.bottom");Q41=makeQuery(id+"F11.boolean.opBoolean","INTERSECT",EDGE,{"derivedFrom":[makeQuery(id+"F9.opFillet","SPLIT",FACE,{"disambiguationData":[OD(1.0)],"derivedFrom":makeQuery(id+"F8.opFillet","MERGE",FACE,{"derivedFrom":[makeQuery(id+"F7.boolean.opBoolean","SPLIT",FACE,{"disambiguationData":[TD([makeQuery(id+"F1.opExtrude","CAP_FACE",FACE,{"disambiguationData":[OSD([subQ22,subQ21,subQ3,subQ16])],"isStart":false})])],"derivedFrom":subQ14}),makeQuery(id+"F7.boolean.opBoolean","SPLIT",FACE,{"disambiguationData":[TD([makeQuery(id+"F1.opExtrude","CAP_FACE",FACE,{"disambiguationData":[OSD([subQ22,subQ21,subQ3,subQ16])],"isStart":true})])],"derivedFrom":subQ14}),makeQuery(id+"F7.boolean.opBoolean","SPLIT",FACE,{"disambiguationData":[TD([subQ17])],"derivedFrom":subQ14}),makeQuery(id+"F7.boolean.opBoolean","SPLIT",FACE,{"disambiguationData":[TD([subQ4])],"derivedFrom":subQ14})]})}),makeQuery(id+"F11.opExtrude","SWEPT_FACE",FACE,{"disambiguationData":[OSD([sQuery(id+"F10.wireOp",EDGE,"E6.0.1.3")])]})]});}
            var Q42;
            {var subQ1=makeQuery(id+"F5.opExtrude","SWEPT_FACE",FACE,{"disambiguationData":[OSD([sQuery(id+"F4.wireOp",EDGE,"E2.top")])]});var subQ2=makeQuery(id+"F3.boolean.opBoolean","COPY",FACE,{"derivedFrom":makeQuery(id+"F3.opExtrude","SWEPT_FACE",FACE,{"disambiguationData":[OSD([sQuery(id+"F2.wireOp",EDGE,"E1.top")])]})});var subQ3=sQuery(id+"F0.wireOp",EDGE,"E0.left");var subQ4=makeQuery(id+"F1.opExtrude","SWEPT_FACE",FACE,{"disambiguationData":[OSD([subQ3])]});var subQ14=makeQuery(id+"F5.boolean.opBoolean","MERGE",FACE,{"derivedFrom":[subQ2,subQ1]});var subQ16=sQuery(id+"F0.wireOp",EDGE,"E0.right");var subQ17=makeQuery(id+"F1.opExtrude","SWEPT_FACE",FACE,{"disambiguationData":[OSD([subQ16])]});var subQ21=sQuery(id+"F0.wireOp",EDGE,"E0.top");var subQ22=sQuery(id+"F0.wireOp",EDGE,"E0.bottom");Q42=makeQuery(id+"F11.boolean.opBoolean","INTERSECT",EDGE,{"derivedFrom":[makeQuery(id+"F9.opFillet","SPLIT",FACE,{"disambiguationData":[OD(2.0)],"derivedFrom":makeQuery(id+"F8.opFillet","MERGE",FACE,{"derivedFrom":[makeQuery(id+"F7.boolean.opBoolean","SPLIT",FACE,{"disambiguationData":[TD([makeQuery(id+"F1.opExtrude","CAP_FACE",FACE,{"disambiguationData":[OSD([subQ22,subQ21,subQ3,subQ16])],"isStart":false})])],"derivedFrom":subQ14}),makeQuery(id+"F7.boolean.opBoolean","SPLIT",FACE,{"disambiguationData":[TD([makeQuery(id+"F1.opExtrude","CAP_FACE",FACE,{"disambiguationData":[OSD([subQ22,subQ21,subQ3,subQ16])],"isStart":true})])],"derivedFrom":subQ14}),makeQuery(id+"F7.boolean.opBoolean","SPLIT",FACE,{"disambiguationData":[TD([subQ17])],"derivedFrom":subQ14}),makeQuery(id+"F7.boolean.opBoolean","SPLIT",FACE,{"disambiguationData":[TD([subQ4])],"derivedFrom":subQ14})]})}),makeQuery(id+"F11.opExtrude","SWEPT_FACE",FACE,{"disambiguationData":[OSD([sQuery(id+"F10.wireOp",EDGE,"E7.top")])]})]});}
            var Q43;
            {var subQ1=makeQuery(id+"F5.opExtrude","SWEPT_FACE",FACE,{"disambiguationData":[OSD([sQuery(id+"F4.wireOp",EDGE,"E2.top")])]});var subQ2=makeQuery(id+"F3.boolean.opBoolean","COPY",FACE,{"derivedFrom":makeQuery(id+"F3.opExtrude","SWEPT_FACE",FACE,{"disambiguationData":[OSD([sQuery(id+"F2.wireOp",EDGE,"E1.top")])]})});var subQ3=sQuery(id+"F0.wireOp",EDGE,"E0.left");var subQ4=makeQuery(id+"F1.opExtrude","SWEPT_FACE",FACE,{"disambiguationData":[OSD([subQ3])]});var subQ14=makeQuery(id+"F5.boolean.opBoolean","MERGE",FACE,{"derivedFrom":[subQ2,subQ1]});var subQ16=sQuery(id+"F0.wireOp",EDGE,"E0.right");var subQ17=makeQuery(id+"F1.opExtrude","SWEPT_FACE",FACE,{"disambiguationData":[OSD([subQ16])]});var subQ21=sQuery(id+"F0.wireOp",EDGE,"E0.top");var subQ22=sQuery(id+"F0.wireOp",EDGE,"E0.bottom");Q43=makeQuery(id+"F11.boolean.opBoolean","INTERSECT",EDGE,{"derivedFrom":[makeQuery(id+"F9.opFillet","SPLIT",FACE,{"disambiguationData":[OD(2.0)],"derivedFrom":makeQuery(id+"F8.opFillet","MERGE",FACE,{"derivedFrom":[makeQuery(id+"F7.boolean.opBoolean","SPLIT",FACE,{"disambiguationData":[TD([makeQuery(id+"F1.opExtrude","CAP_FACE",FACE,{"disambiguationData":[OSD([subQ22,subQ21,subQ3,subQ16])],"isStart":false})])],"derivedFrom":subQ14}),makeQuery(id+"F7.boolean.opBoolean","SPLIT",FACE,{"disambiguationData":[TD([makeQuery(id+"F1.opExtrude","CAP_FACE",FACE,{"disambiguationData":[OSD([subQ22,subQ21,subQ3,subQ16])],"isStart":true})])],"derivedFrom":subQ14}),makeQuery(id+"F7.boolean.opBoolean","SPLIT",FACE,{"disambiguationData":[TD([subQ17])],"derivedFrom":subQ14}),makeQuery(id+"F7.boolean.opBoolean","SPLIT",FACE,{"disambiguationData":[TD([subQ4])],"derivedFrom":subQ14})]})}),makeQuery(id+"F11.opExtrude","SWEPT_FACE",FACE,{"disambiguationData":[OSD([sQuery(id+"F10.wireOp",EDGE,"E8.0.1.0")])]})]});}
            var Q44;
            {var subQ1=makeQuery(id+"F5.opExtrude","SWEPT_FACE",FACE,{"disambiguationData":[OSD([sQuery(id+"F4.wireOp",EDGE,"E2.top")])]});var subQ2=makeQuery(id+"F3.boolean.opBoolean","COPY",FACE,{"derivedFrom":makeQuery(id+"F3.opExtrude","SWEPT_FACE",FACE,{"disambiguationData":[OSD([sQuery(id+"F2.wireOp",EDGE,"E1.top")])]})});var subQ3=sQuery(id+"F0.wireOp",EDGE,"E0.left");var subQ4=makeQuery(id+"F1.opExtrude","SWEPT_FACE",FACE,{"disambiguationData":[OSD([subQ3])]});var subQ14=makeQuery(id+"F5.boolean.opBoolean","MERGE",FACE,{"derivedFrom":[subQ2,subQ1]});var subQ16=sQuery(id+"F0.wireOp",EDGE,"E0.right");var subQ17=makeQuery(id+"F1.opExtrude","SWEPT_FACE",FACE,{"disambiguationData":[OSD([subQ16])]});var subQ21=sQuery(id+"F0.wireOp",EDGE,"E0.top");var subQ22=sQuery(id+"F0.wireOp",EDGE,"E0.bottom");Q44=makeQuery(id+"F11.boolean.opBoolean","INTERSECT",EDGE,{"derivedFrom":[makeQuery(id+"F9.opFillet","SPLIT",FACE,{"disambiguationData":[OD(2.0)],"derivedFrom":makeQuery(id+"F8.opFillet","MERGE",FACE,{"derivedFrom":[makeQuery(id+"F7.boolean.opBoolean","SPLIT",FACE,{"disambiguationData":[TD([makeQuery(id+"F1.opExtrude","CAP_FACE",FACE,{"disambiguationData":[OSD([subQ22,subQ21,subQ3,subQ16])],"isStart":false})])],"derivedFrom":subQ14}),makeQuery(id+"F7.boolean.opBoolean","SPLIT",FACE,{"disambiguationData":[TD([makeQuery(id+"F1.opExtrude","CAP_FACE",FACE,{"disambiguationData":[OSD([subQ22,subQ21,subQ3,subQ16])],"isStart":true})])],"derivedFrom":subQ14}),makeQuery(id+"F7.boolean.opBoolean","SPLIT",FACE,{"disambiguationData":[TD([subQ17])],"derivedFrom":subQ14}),makeQuery(id+"F7.boolean.opBoolean","SPLIT",FACE,{"disambiguationData":[TD([subQ4])],"derivedFrom":subQ14})]})}),makeQuery(id+"F11.opExtrude","SWEPT_FACE",FACE,{"disambiguationData":[OSD([sQuery(id+"F10.wireOp",EDGE,"E8.0.2.0")])]})]});}
            var Q45;
            {var subQ0=makeQuery(id+"F5.opExtrude","SWEPT_FACE",FACE,{"disambiguationData":[OSD([sQuery(id+"F4.wireOp",EDGE,"E2.bottom")])]});var subQ2=makeQuery(id+"F3.boolean.opBoolean","COPY",FACE,{"derivedFrom":makeQuery(id+"F3.opExtrude","SWEPT_FACE",FACE,{"disambiguationData":[OSD([sQuery(id+"F2.wireOp",EDGE,"E1.bottom")])]})});var subQ3=sQuery(id+"F0.wireOp",EDGE,"E0.left");var subQ4=makeQuery(id+"F1.opExtrude","SWEPT_FACE",FACE,{"disambiguationData":[OSD([subQ3])]});var subQ14=makeQuery(id+"F5.boolean.opBoolean","MERGE",FACE,{"derivedFrom":[subQ2,subQ0]});var subQ16=sQuery(id+"F0.wireOp",EDGE,"E0.right");var subQ17=makeQuery(id+"F1.opExtrude","SWEPT_FACE",FACE,{"disambiguationData":[OSD([subQ16])]});var subQ21=sQuery(id+"F0.wireOp",EDGE,"E0.top");var subQ22=sQuery(id+"F0.wireOp",EDGE,"E0.bottom");Q45=makeQuery(id+"F11.boolean.opBoolean","INTERSECT",EDGE,{"derivedFrom":[makeQuery(id+"F9.opFillet","SPLIT",FACE,{"disambiguationData":[OD(2.0)],"derivedFrom":makeQuery(id+"F8.opFillet","MERGE",FACE,{"derivedFrom":[makeQuery(id+"F7.boolean.opBoolean","SPLIT",FACE,{"disambiguationData":[TD([makeQuery(id+"F1.opExtrude","CAP_FACE",FACE,{"disambiguationData":[OSD([subQ22,subQ21,subQ3,subQ16])],"isStart":false})])],"derivedFrom":subQ14}),makeQuery(id+"F7.boolean.opBoolean","SPLIT",FACE,{"disambiguationData":[TD([makeQuery(id+"F1.opExtrude","CAP_FACE",FACE,{"disambiguationData":[OSD([subQ22,subQ21,subQ3,subQ16])],"isStart":true})])],"derivedFrom":subQ14}),makeQuery(id+"F7.boolean.opBoolean","SPLIT",FACE,{"disambiguationData":[TD([subQ17])],"derivedFrom":subQ14}),makeQuery(id+"F7.boolean.opBoolean","SPLIT",FACE,{"disambiguationData":[TD([subQ4])],"derivedFrom":subQ14})]})}),makeQuery(id+"F11.opExtrude","SWEPT_FACE",FACE,{"disambiguationData":[OSD([sQuery(id+"F10.wireOp",EDGE,"E7.top")])]})]});}
            var Q46;
            {var subQ0=makeQuery(id+"F5.opExtrude","SWEPT_FACE",FACE,{"disambiguationData":[OSD([sQuery(id+"F4.wireOp",EDGE,"E2.bottom")])]});var subQ2=makeQuery(id+"F3.boolean.opBoolean","COPY",FACE,{"derivedFrom":makeQuery(id+"F3.opExtrude","SWEPT_FACE",FACE,{"disambiguationData":[OSD([sQuery(id+"F2.wireOp",EDGE,"E1.bottom")])]})});var subQ3=sQuery(id+"F0.wireOp",EDGE,"E0.left");var subQ4=makeQuery(id+"F1.opExtrude","SWEPT_FACE",FACE,{"disambiguationData":[OSD([subQ3])]});var subQ14=makeQuery(id+"F5.boolean.opBoolean","MERGE",FACE,{"derivedFrom":[subQ2,subQ0]});var subQ16=sQuery(id+"F0.wireOp",EDGE,"E0.right");var subQ17=makeQuery(id+"F1.opExtrude","SWEPT_FACE",FACE,{"disambiguationData":[OSD([subQ16])]});var subQ21=sQuery(id+"F0.wireOp",EDGE,"E0.top");var subQ22=sQuery(id+"F0.wireOp",EDGE,"E0.bottom");Q46=makeQuery(id+"F11.boolean.opBoolean","INTERSECT",EDGE,{"derivedFrom":[makeQuery(id+"F9.opFillet","SPLIT",FACE,{"disambiguationData":[OD(2.0)],"derivedFrom":makeQuery(id+"F8.opFillet","MERGE",FACE,{"derivedFrom":[makeQuery(id+"F7.boolean.opBoolean","SPLIT",FACE,{"disambiguationData":[TD([makeQuery(id+"F1.opExtrude","CAP_FACE",FACE,{"disambiguationData":[OSD([subQ22,subQ21,subQ3,subQ16])],"isStart":false})])],"derivedFrom":subQ14}),makeQuery(id+"F7.boolean.opBoolean","SPLIT",FACE,{"disambiguationData":[TD([makeQuery(id+"F1.opExtrude","CAP_FACE",FACE,{"disambiguationData":[OSD([subQ22,subQ21,subQ3,subQ16])],"isStart":true})])],"derivedFrom":subQ14}),makeQuery(id+"F7.boolean.opBoolean","SPLIT",FACE,{"disambiguationData":[TD([subQ17])],"derivedFrom":subQ14}),makeQuery(id+"F7.boolean.opBoolean","SPLIT",FACE,{"disambiguationData":[TD([subQ4])],"derivedFrom":subQ14})]})}),makeQuery(id+"F11.opExtrude","SWEPT_FACE",FACE,{"disambiguationData":[OSD([sQuery(id+"F10.wireOp",EDGE,"E8.0.1.0")])]})]});}
            var Q47;
            {var subQ0=makeQuery(id+"F5.opExtrude","SWEPT_FACE",FACE,{"disambiguationData":[OSD([sQuery(id+"F4.wireOp",EDGE,"E2.bottom")])]});var subQ2=makeQuery(id+"F3.boolean.opBoolean","COPY",FACE,{"derivedFrom":makeQuery(id+"F3.opExtrude","SWEPT_FACE",FACE,{"disambiguationData":[OSD([sQuery(id+"F2.wireOp",EDGE,"E1.bottom")])]})});var subQ3=sQuery(id+"F0.wireOp",EDGE,"E0.left");var subQ4=makeQuery(id+"F1.opExtrude","SWEPT_FACE",FACE,{"disambiguationData":[OSD([subQ3])]});var subQ14=makeQuery(id+"F5.boolean.opBoolean","MERGE",FACE,{"derivedFrom":[subQ2,subQ0]});var subQ16=sQuery(id+"F0.wireOp",EDGE,"E0.right");var subQ17=makeQuery(id+"F1.opExtrude","SWEPT_FACE",FACE,{"disambiguationData":[OSD([subQ16])]});var subQ21=sQuery(id+"F0.wireOp",EDGE,"E0.top");var subQ22=sQuery(id+"F0.wireOp",EDGE,"E0.bottom");Q47=makeQuery(id+"F11.boolean.opBoolean","INTERSECT",EDGE,{"derivedFrom":[makeQuery(id+"F9.opFillet","SPLIT",FACE,{"disambiguationData":[OD(2.0)],"derivedFrom":makeQuery(id+"F8.opFillet","MERGE",FACE,{"derivedFrom":[makeQuery(id+"F7.boolean.opBoolean","SPLIT",FACE,{"disambiguationData":[TD([makeQuery(id+"F1.opExtrude","CAP_FACE",FACE,{"disambiguationData":[OSD([subQ22,subQ21,subQ3,subQ16])],"isStart":false})])],"derivedFrom":subQ14}),makeQuery(id+"F7.boolean.opBoolean","SPLIT",FACE,{"disambiguationData":[TD([makeQuery(id+"F1.opExtrude","CAP_FACE",FACE,{"disambiguationData":[OSD([subQ22,subQ21,subQ3,subQ16])],"isStart":true})])],"derivedFrom":subQ14}),makeQuery(id+"F7.boolean.opBoolean","SPLIT",FACE,{"disambiguationData":[TD([subQ17])],"derivedFrom":subQ14}),makeQuery(id+"F7.boolean.opBoolean","SPLIT",FACE,{"disambiguationData":[TD([subQ4])],"derivedFrom":subQ14})]})}),makeQuery(id+"F11.opExtrude","SWEPT_FACE",FACE,{"disambiguationData":[OSD([sQuery(id+"F10.wireOp",EDGE,"E8.0.2.0")])]})]});}
            fillet(context, id + "F12", {"entities" : qUnion([Q0, Q1, Q2, Q3, Q4, Q5, Q6, Q7, Q8, Q9, Q10, Q11, Q12, Q13, Q14, Q15, Q16, Q17, Q18, Q19, Q20, Q21, Q22, Q23, Q24, Q25, Q26, Q27, Q28, Q29, Q30, Q31, Q32, Q33, Q34, Q35, Q36, Q37, Q38, Q39, Q40, Q41, Q42, Q43, Q44, Q45, Q46, Q47]), "radius" : 2 * mm, "tangentPropagation" : true, "allowEdgeOverflow" : false});
        }
    });
